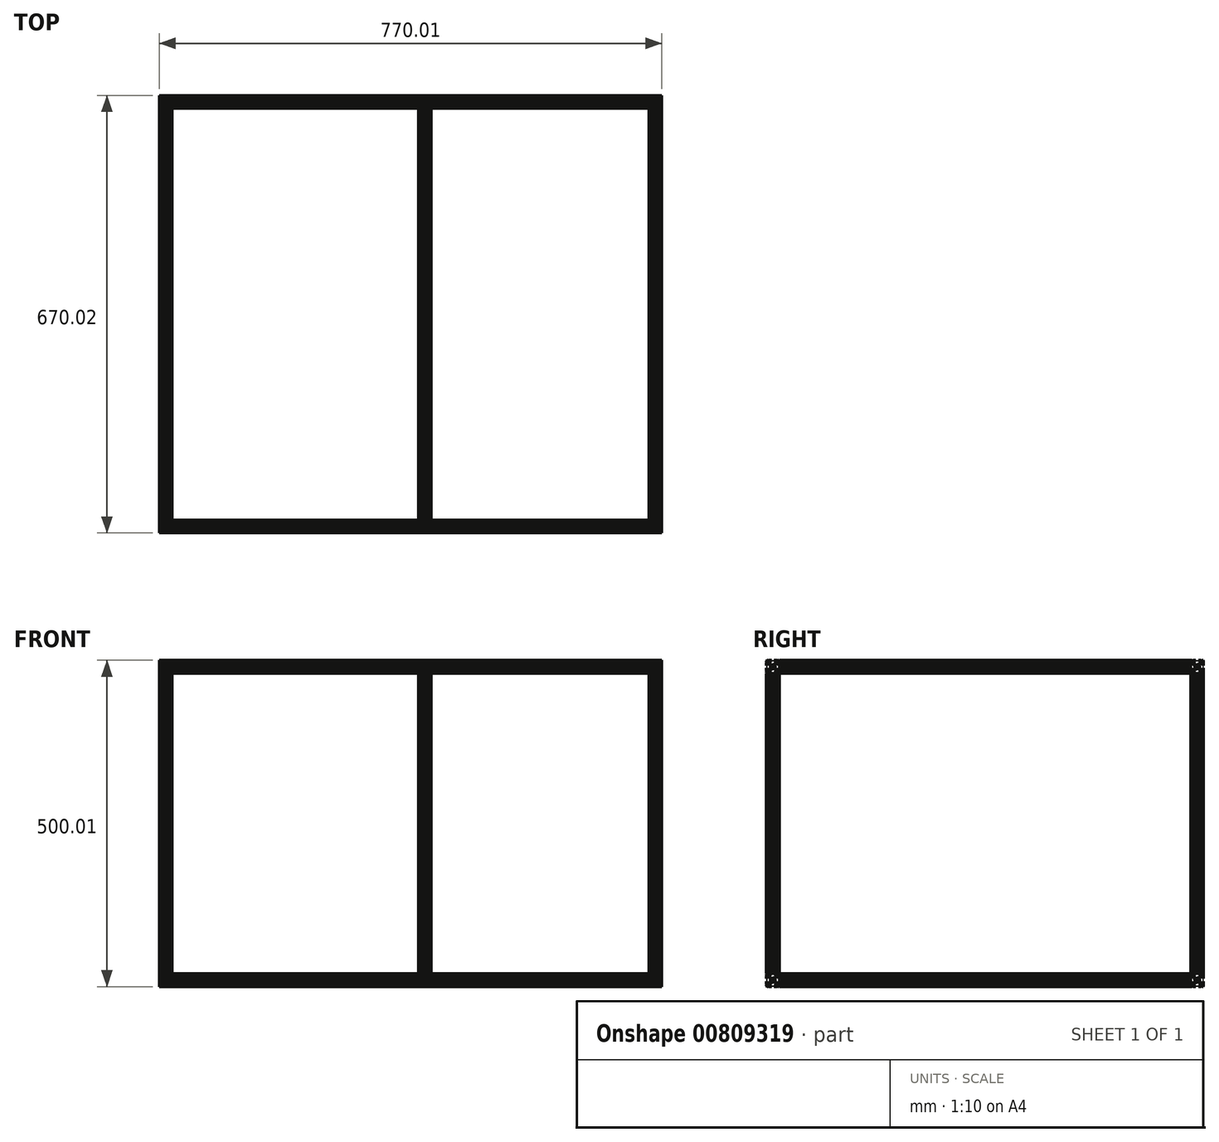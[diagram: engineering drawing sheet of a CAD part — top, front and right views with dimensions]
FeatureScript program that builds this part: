
annotation { "Feature Type Name" : "Feature", "Feature Type Description" : "" }
export const myFeature = defineFeature(function(context is Context, id is Id, definition is map)
    precondition{}
    {
        {
            var Q0;
            Q0=qCreatedBy(makeId("Right.planeOp"),FACE);
            var sketch = newSketch(context, id + "F0", { "sketchPlane" : qUnion([Q0])});
            skLineSegment(sketch, "E0", {"start": v(25.7, -17.22) * mm, "end": v(25.7, -25.12) * mm});
            skLineSegment(sketch, "E1", {"start": v(22.1, -21.63) * mm, "end": v(30.9, -21.63) * mm});
            skLineSegment(sketch, "E2", {"start": v(25.7, -40.02) * mm, "end": v(25.7, -32.12) * mm});
            skLineSegment(sketch, "E3", {"start": v(22.1, -35.63) * mm, "end": v(30.9, -35.63) * mm});
            skLineSegment(sketch, "E4", {"start": v(28.7, -30.77) * mm, "end": v(27.2, -30.77) * mm});
            skLineSegment(sketch, "E5", {"start": v(27.2, -32.77) * mm, "end": v(23.2, -32.77) * mm});
            skLineSegment(sketch, "E6", {"start": v(27.2, -32.77) * mm, "end": v(27.2, -30.77) * mm});
            skLineSegment(sketch, "E7", {"start": v(28.7, -26.48) * mm, "end": v(27.2, -26.48) * mm});
            skLineSegment(sketch, "E8", {"start": v(27.2, -24.48) * mm, "end": v(23.2, -24.48) * mm});
            skLineSegment(sketch, "E9", {"start": v(27.2, -24.48) * mm, "end": v(27.2, -26.48) * mm});
            skLineSegment(sketch, "E10", {"start": v(23.2, -24.48) * mm, "end": v(23.2, -26.12) * mm});
            skLineSegment(sketch, "E11", {"start": v(23.2, -26.12) * mm, "end": v(21.9, -26.12) * mm});
            skLineSegment(sketch, "E12", {"start": v(23.2, -32.77) * mm, "end": v(21.9, -26.12) * mm});
            skLineSegment(sketch, "E13", {"start": v(27.34, -20.94) * mm, "end": v(26.38, -19.97) * mm});
            skLineSegment(sketch, "E14", {"start": v(26.38, -19.97) * mm, "end": v(25, -19.97) * mm});
            skLineSegment(sketch, "E15", {"start": v(25, -19.97) * mm, "end": v(24.04, -20.94) * mm});
            skLineSegment(sketch, "E16", {"start": v(24.04, -20.94) * mm, "end": v(24.04, -22.3) * mm});
            skLineSegment(sketch, "E17", {"start": v(24.04, -22.3) * mm, "end": v(25, -23.28) * mm});
            skLineSegment(sketch, "E18", {"start": v(25, -23.28) * mm, "end": v(26.38, -23.28) * mm});
            skLineSegment(sketch, "E19", {"start": v(26.38, -23.28) * mm, "end": v(27.34, -22.3) * mm});
            skLineSegment(sketch, "E20", {"start": v(27.34, -22.3) * mm, "end": v(27.34, -20.94) * mm});
            skLineSegment(sketch, "E21", {"start": v(27.34, -34.94) * mm, "end": v(26.38, -33.98) * mm});
            skLineSegment(sketch, "E22", {"start": v(26.38, -33.98) * mm, "end": v(25, -33.98) * mm});
            skLineSegment(sketch, "E23", {"start": v(25, -33.98) * mm, "end": v(24.04, -34.94) * mm});
            skLineSegment(sketch, "E24", {"start": v(24.04, -34.94) * mm, "end": v(24.04, -36.3) * mm});
            skLineSegment(sketch, "E25", {"start": v(24.04, -36.3) * mm, "end": v(25, -37.28) * mm});
            skLineSegment(sketch, "E26", {"start": v(25, -37.28) * mm, "end": v(26.38, -37.28) * mm});
            skLineSegment(sketch, "E27", {"start": v(26.38, -37.28) * mm, "end": v(27.34, -36.3) * mm});
            skLineSegment(sketch, "E28", {"start": v(27.34, -36.3) * mm, "end": v(27.34, -34.94) * mm});
            skLineSegment(sketch, "E29", {"start": v(27.7, -18.62) * mm, "end": v(28.7, -19.62) * mm});
            skLineSegment(sketch, "E30", {"start": v(28.7, -37.62) * mm, "end": v(27.7, -38.62) * mm});
            skLineSegment(sketch, "E31", {"start": v(25.7, -18.83) * mm, "end": v(26.44, -18.83) * mm});
            skLineSegment(sketch, "E32", {"start": v(26.44, -18.83) * mm, "end": v(26.44, -18.62) * mm});
            skLineSegment(sketch, "E33", {"start": v(25.7, -18.83) * mm, "end": v(24.94, -18.83) * mm});
            skLineSegment(sketch, "E34", {"start": v(24.94, -18.83) * mm, "end": v(24.94, -18.62) * mm});
            skLineSegment(sketch, "E35", {"start": v(27.7, -18.62) * mm, "end": v(26.44, -18.62) * mm});
            skLineSegment(sketch, "E36", {"start": v(28.5, -21.63) * mm, "end": v(28.5, -22.38) * mm});
            skLineSegment(sketch, "E37", {"start": v(28.5, -22.38) * mm, "end": v(28.7, -22.38) * mm});
            skLineSegment(sketch, "E38", {"start": v(28.5, -21.63) * mm, "end": v(28.5, -20.88) * mm});
            skLineSegment(sketch, "E39", {"start": v(28.5, -20.88) * mm, "end": v(28.7, -20.88) * mm});
            skLineSegment(sketch, "E40", {"start": v(28.5, -35.63) * mm, "end": v(28.5, -34.88) * mm});
            skLineSegment(sketch, "E41", {"start": v(28.5, -34.88) * mm, "end": v(28.7, -34.88) * mm});
            skLineSegment(sketch, "E42", {"start": v(28.5, -35.63) * mm, "end": v(28.5, -36.38) * mm});
            skLineSegment(sketch, "E43", {"start": v(28.5, -36.38) * mm, "end": v(28.7, -36.38) * mm});
            skLineSegment(sketch, "E44", {"start": v(25.7, -38.43) * mm, "end": v(26.44, -38.43) * mm});
            skLineSegment(sketch, "E45", {"start": v(26.44, -38.43) * mm, "end": v(26.44, -38.62) * mm});
            skLineSegment(sketch, "E46", {"start": v(25.7, -38.43) * mm, "end": v(24.94, -38.43) * mm});
            skLineSegment(sketch, "E47", {"start": v(24.94, -38.43) * mm, "end": v(24.94, -38.62) * mm});
            skLineSegment(sketch, "E48", {"start": v(28.7, -19.62) * mm, "end": v(28.7, -20.88) * mm});
            skLineSegment(sketch, "E49", {"start": v(28.7, -22.38) * mm, "end": v(28.7, -26.48) * mm});
            skLineSegment(sketch, "E50", {"start": v(27.7, -38.62) * mm, "end": v(26.44, -38.62) * mm});
            skLineSegment(sketch, "E51", {"start": v(28.7, -37.62) * mm, "end": v(28.7, -36.38) * mm});
            skLineSegment(sketch, "E52", {"start": v(28.7, -34.88) * mm, "end": v(28.7, -30.77) * mm});
            skLineSegment(sketch, "E53", {"start": v(18.7, -13.92) * mm, "end": v(18.7, -42.92) * mm});
            skLineSegment(sketch, "E54", {"start": v(20.84, -18.62) * mm, "end": v(20.84, -20.12) * mm});
            skLineSegment(sketch, "E55", {"start": v(22.84, -20.12) * mm, "end": v(22.84, -24.12) * mm});
            skLineSegment(sketch, "E56", {"start": v(22.84, -20.12) * mm, "end": v(20.84, -20.12) * mm});
            skLineSegment(sketch, "E57", {"start": v(16.54, -18.62) * mm, "end": v(16.54, -20.12) * mm});
            skLineSegment(sketch, "E58", {"start": v(14.54, -20.12) * mm, "end": v(14.54, -24.12) * mm});
            skLineSegment(sketch, "E59", {"start": v(14.54, -20.12) * mm, "end": v(16.54, -20.12) * mm});
            skLineSegment(sketch, "E60", {"start": v(14.54, -24.12) * mm, "end": v(16.2, -24.12) * mm});
            skLineSegment(sketch, "E61", {"start": v(16.2, -24.12) * mm, "end": v(16.2, -25.42) * mm});
            skLineSegment(sketch, "E62", {"start": v(22.84, -24.12) * mm, "end": v(16.2, -25.42) * mm});
            skLineSegment(sketch, "E63", {"start": v(16.54, -38.62) * mm, "end": v(16.54, -37.12) * mm});
            skLineSegment(sketch, "E64", {"start": v(14.54, -37.12) * mm, "end": v(14.54, -33.12) * mm});
            skLineSegment(sketch, "E65", {"start": v(14.54, -37.12) * mm, "end": v(16.54, -37.12) * mm});
            skLineSegment(sketch, "E66", {"start": v(20.84, -38.62) * mm, "end": v(20.84, -37.12) * mm});
            skLineSegment(sketch, "E67", {"start": v(22.84, -37.12) * mm, "end": v(22.84, -33.12) * mm});
            skLineSegment(sketch, "E68", {"start": v(22.84, -37.12) * mm, "end": v(20.84, -37.12) * mm});
            skLineSegment(sketch, "E69", {"start": v(22.84, -33.12) * mm, "end": v(21.2, -33.12) * mm});
            skLineSegment(sketch, "E70", {"start": v(21.2, -33.12) * mm, "end": v(21.2, -31.83) * mm});
            skLineSegment(sketch, "E71", {"start": v(14.54, -33.12) * mm, "end": v(21.2, -31.83) * mm});
            skLineSegment(sketch, "E72", {"start": v(24.94, -18.62) * mm, "end": v(20.84, -18.62) * mm});
            skLineSegment(sketch, "E73", {"start": v(24.94, -38.62) * mm, "end": v(20.84, -38.62) * mm});
            skLineSegment(sketch, "E74", {"start": v(6.1, -28.62) * mm, "end": v(31.6, -28.62) * mm});
            skLineSegment(sketch, "E75", {"start": v(11.7, -17.22) * mm, "end": v(11.7, -25.12) * mm});
            skLineSegment(sketch, "E76", {"start": v(15.3, -21.63) * mm, "end": v(6.5, -21.63) * mm});
            skLineSegment(sketch, "E77", {"start": v(10.04, -20.94) * mm, "end": v(11, -19.97) * mm});
            skLineSegment(sketch, "E78", {"start": v(11, -19.97) * mm, "end": v(12.38, -19.97) * mm});
            skLineSegment(sketch, "E79", {"start": v(12.38, -19.97) * mm, "end": v(13.34, -20.94) * mm});
            skLineSegment(sketch, "E80", {"start": v(13.34, -20.94) * mm, "end": v(13.34, -22.3) * mm});
            skLineSegment(sketch, "E81", {"start": v(13.34, -22.3) * mm, "end": v(12.38, -23.28) * mm});
            skLineSegment(sketch, "E82", {"start": v(12.38, -23.28) * mm, "end": v(11, -23.28) * mm});
            skLineSegment(sketch, "E83", {"start": v(11, -23.28) * mm, "end": v(10.04, -22.3) * mm});
            skLineSegment(sketch, "E84", {"start": v(10.04, -22.3) * mm, "end": v(10.04, -20.94) * mm});
            skLineSegment(sketch, "E85", {"start": v(9.7, -18.62) * mm, "end": v(8.7, -19.62) * mm});
            skLineSegment(sketch, "E86", {"start": v(11.7, -18.83) * mm, "end": v(10.94, -18.83) * mm});
            skLineSegment(sketch, "E87", {"start": v(10.94, -18.83) * mm, "end": v(10.94, -18.62) * mm});
            skLineSegment(sketch, "E88", {"start": v(11.7, -18.83) * mm, "end": v(12.44, -18.83) * mm});
            skLineSegment(sketch, "E89", {"start": v(12.44, -18.83) * mm, "end": v(12.44, -18.62) * mm});
            skLineSegment(sketch, "E90", {"start": v(9.7, -18.62) * mm, "end": v(10.94, -18.62) * mm});
            skLineSegment(sketch, "E91", {"start": v(8.9, -21.63) * mm, "end": v(8.9, -22.38) * mm});
            skLineSegment(sketch, "E92", {"start": v(8.9, -22.38) * mm, "end": v(8.7, -22.38) * mm});
            skLineSegment(sketch, "E93", {"start": v(8.9, -21.63) * mm, "end": v(8.9, -20.88) * mm});
            skLineSegment(sketch, "E94", {"start": v(8.9, -20.88) * mm, "end": v(8.7, -20.88) * mm});
            skLineSegment(sketch, "E95", {"start": v(8.7, -19.62) * mm, "end": v(8.7, -20.88) * mm});
            skLineSegment(sketch, "E96", {"start": v(8.7, -22.38) * mm, "end": v(8.7, -26.48) * mm});
            skLineSegment(sketch, "E97", {"start": v(12.44, -18.62) * mm, "end": v(16.54, -18.62) * mm});
            skLineSegment(sketch, "E98", {"start": v(11.7, -40.02) * mm, "end": v(11.7, -32.12) * mm});
            skLineSegment(sketch, "E99", {"start": v(15.3, -35.63) * mm, "end": v(6.5, -35.63) * mm});
            skLineSegment(sketch, "E100", {"start": v(10.04, -34.94) * mm, "end": v(11, -33.98) * mm});
            skLineSegment(sketch, "E101", {"start": v(11, -33.98) * mm, "end": v(12.38, -33.98) * mm});
            skLineSegment(sketch, "E102", {"start": v(12.38, -33.98) * mm, "end": v(13.34, -34.94) * mm});
            skLineSegment(sketch, "E103", {"start": v(13.34, -34.94) * mm, "end": v(13.34, -36.3) * mm});
            skLineSegment(sketch, "E104", {"start": v(13.34, -36.3) * mm, "end": v(12.38, -37.28) * mm});
            skLineSegment(sketch, "E105", {"start": v(12.38, -37.28) * mm, "end": v(11, -37.28) * mm});
            skLineSegment(sketch, "E106", {"start": v(11, -37.28) * mm, "end": v(10.04, -36.3) * mm});
            skLineSegment(sketch, "E107", {"start": v(10.04, -36.3) * mm, "end": v(10.04, -34.94) * mm});
            skLineSegment(sketch, "E108", {"start": v(8.7, -37.62) * mm, "end": v(9.7, -38.62) * mm});
            skLineSegment(sketch, "E109", {"start": v(8.9, -35.63) * mm, "end": v(8.9, -34.88) * mm});
            skLineSegment(sketch, "E110", {"start": v(8.9, -34.88) * mm, "end": v(8.7, -34.88) * mm});
            skLineSegment(sketch, "E111", {"start": v(8.9, -35.63) * mm, "end": v(8.9, -36.38) * mm});
            skLineSegment(sketch, "E112", {"start": v(8.9, -36.38) * mm, "end": v(8.7, -36.38) * mm});
            skLineSegment(sketch, "E113", {"start": v(11.7, -38.43) * mm, "end": v(10.94, -38.43) * mm});
            skLineSegment(sketch, "E114", {"start": v(10.94, -38.43) * mm, "end": v(10.94, -38.62) * mm});
            skLineSegment(sketch, "E115", {"start": v(11.7, -38.43) * mm, "end": v(12.44, -38.43) * mm});
            skLineSegment(sketch, "E116", {"start": v(12.44, -38.43) * mm, "end": v(12.44, -38.62) * mm});
            skLineSegment(sketch, "E117", {"start": v(9.7, -38.62) * mm, "end": v(10.94, -38.62) * mm});
            skLineSegment(sketch, "E118", {"start": v(8.7, -37.62) * mm, "end": v(8.7, -36.38) * mm});
            skLineSegment(sketch, "E119", {"start": v(8.7, -34.88) * mm, "end": v(8.7, -30.77) * mm});
            skLineSegment(sketch, "E120", {"start": v(12.44, -38.62) * mm, "end": v(16.54, -38.62) * mm});
            skLineSegment(sketch, "E121", {"start": v(8.7, -26.48) * mm, "end": v(10.2, -26.48) * mm});
            skLineSegment(sketch, "E122", {"start": v(10.2, -24.48) * mm, "end": v(14.2, -24.48) * mm});
            skLineSegment(sketch, "E123", {"start": v(10.2, -24.48) * mm, "end": v(10.2, -26.48) * mm});
            skLineSegment(sketch, "E124", {"start": v(8.7, -30.77) * mm, "end": v(10.2, -30.77) * mm});
            skLineSegment(sketch, "E125", {"start": v(10.2, -32.77) * mm, "end": v(14.2, -32.77) * mm});
            skLineSegment(sketch, "E126", {"start": v(10.2, -32.77) * mm, "end": v(10.2, -30.77) * mm});
            skLineSegment(sketch, "E127", {"start": v(14.2, -32.77) * mm, "end": v(14.2, -31.12) * mm});
            skLineSegment(sketch, "E128", {"start": v(14.2, -31.12) * mm, "end": v(15.5, -31.12) * mm});
            skLineSegment(sketch, "E129", {"start": v(14.2, -24.48) * mm, "end": v(15.5, -31.12) * mm});
            skCircle(sketch, "E130", {"center": v(18.7, -28.62) * mm, "radius": 1.6 * mm});
            skSolve(sketch);
        }
        {
            var Q0;
            Q0 = qSketchRegion(id + "F0", true);
            extrude(context, id + "F1", {"entities" : qUnion([Q0]), "oppositeDirection" : true, "depth" : 770 * mm, "offsetDistance" : 25 * mm});
        }
        {
            var Q0;
            Q0=makeQuery(id+"F1.opExtrude","SWEPT_BODY",BODY,{"disambiguationData":[OSD([sQuery(id+"F0.wireOp",EDGE,"E4"),sQuery(id+"F0.wireOp",EDGE,"E5"),sQuery(id+"F0.wireOp",EDGE,"E6"),sQuery(id+"F0.wireOp",EDGE,"E7"),sQuery(id+"F0.wireOp",EDGE,"E8"),sQuery(id+"F0.wireOp",EDGE,"E9"),sQuery(id+"F0.wireOp",EDGE,"E10"),sQuery(id+"F0.wireOp",EDGE,"E11"),sQuery(id+"F0.wireOp",EDGE,"E12"),sQuery(id+"F0.wireOp",EDGE,"E13"),sQuery(id+"F0.wireOp",EDGE,"E14"),sQuery(id+"F0.wireOp",EDGE,"E15"),sQuery(id+"F0.wireOp",EDGE,"E16"),sQuery(id+"F0.wireOp",EDGE,"E17"),sQuery(id+"F0.wireOp",EDGE,"E18"),sQuery(id+"F0.wireOp",EDGE,"E19"),sQuery(id+"F0.wireOp",EDGE,"E20"),sQuery(id+"F0.wireOp",EDGE,"E21"),sQuery(id+"F0.wireOp",EDGE,"E22"),sQuery(id+"F0.wireOp",EDGE,"E23"),sQuery(id+"F0.wireOp",EDGE,"E24"),sQuery(id+"F0.wireOp",EDGE,"E25"),sQuery(id+"F0.wireOp",EDGE,"E26"),sQuery(id+"F0.wireOp",EDGE,"E27"),sQuery(id+"F0.wireOp",EDGE,"E28"),sQuery(id+"F0.wireOp",EDGE,"E29"),sQuery(id+"F0.wireOp",EDGE,"E30"),sQuery(id+"F0.wireOp",EDGE,"E31"),sQuery(id+"F0.wireOp",EDGE,"E32"),sQuery(id+"F0.wireOp",EDGE,"E33"),sQuery(id+"F0.wireOp",EDGE,"E34"),sQuery(id+"F0.wireOp",EDGE,"E35"),sQuery(id+"F0.wireOp",EDGE,"E36"),sQuery(id+"F0.wireOp",EDGE,"E37"),sQuery(id+"F0.wireOp",EDGE,"E38"),sQuery(id+"F0.wireOp",EDGE,"E39"),sQuery(id+"F0.wireOp",EDGE,"E40"),sQuery(id+"F0.wireOp",EDGE,"E41"),sQuery(id+"F0.wireOp",EDGE,"E42"),sQuery(id+"F0.wireOp",EDGE,"E43"),sQuery(id+"F0.wireOp",EDGE,"E44"),sQuery(id+"F0.wireOp",EDGE,"E45"),sQuery(id+"F0.wireOp",EDGE,"E46"),sQuery(id+"F0.wireOp",EDGE,"E47"),sQuery(id+"F0.wireOp",EDGE,"E48"),sQuery(id+"F0.wireOp",EDGE,"E49"),sQuery(id+"F0.wireOp",EDGE,"E50"),sQuery(id+"F0.wireOp",EDGE,"E51"),sQuery(id+"F0.wireOp",EDGE,"E52"),sQuery(id+"F0.wireOp",EDGE,"E54"),sQuery(id+"F0.wireOp",EDGE,"E55"),sQuery(id+"F0.wireOp",EDGE,"E56"),sQuery(id+"F0.wireOp",EDGE,"E57"),sQuery(id+"F0.wireOp",EDGE,"E58"),sQuery(id+"F0.wireOp",EDGE,"E59"),sQuery(id+"F0.wireOp",EDGE,"E60"),sQuery(id+"F0.wireOp",EDGE,"E61"),sQuery(id+"F0.wireOp",EDGE,"E62"),sQuery(id+"F0.wireOp",EDGE,"E63"),sQuery(id+"F0.wireOp",EDGE,"E64"),sQuery(id+"F0.wireOp",EDGE,"E65"),sQuery(id+"F0.wireOp",EDGE,"E66"),sQuery(id+"F0.wireOp",EDGE,"E67"),sQuery(id+"F0.wireOp",EDGE,"E68"),sQuery(id+"F0.wireOp",EDGE,"E69"),sQuery(id+"F0.wireOp",EDGE,"E70"),sQuery(id+"F0.wireOp",EDGE,"E71"),sQuery(id+"F0.wireOp",EDGE,"E72"),sQuery(id+"F0.wireOp",EDGE,"E73"),sQuery(id+"F0.wireOp",EDGE,"E77"),sQuery(id+"F0.wireOp",EDGE,"E78"),sQuery(id+"F0.wireOp",EDGE,"E79"),sQuery(id+"F0.wireOp",EDGE,"E80"),sQuery(id+"F0.wireOp",EDGE,"E81"),sQuery(id+"F0.wireOp",EDGE,"E82"),sQuery(id+"F0.wireOp",EDGE,"E83"),sQuery(id+"F0.wireOp",EDGE,"E84"),sQuery(id+"F0.wireOp",EDGE,"E85"),sQuery(id+"F0.wireOp",EDGE,"E86"),sQuery(id+"F0.wireOp",EDGE,"E87"),sQuery(id+"F0.wireOp",EDGE,"E88"),sQuery(id+"F0.wireOp",EDGE,"E89"),sQuery(id+"F0.wireOp",EDGE,"E90"),sQuery(id+"F0.wireOp",EDGE,"E91"),sQuery(id+"F0.wireOp",EDGE,"E92"),sQuery(id+"F0.wireOp",EDGE,"E93"),sQuery(id+"F0.wireOp",EDGE,"E94"),sQuery(id+"F0.wireOp",EDGE,"E95"),sQuery(id+"F0.wireOp",EDGE,"E96"),sQuery(id+"F0.wireOp",EDGE,"E97"),sQuery(id+"F0.wireOp",EDGE,"E100"),sQuery(id+"F0.wireOp",EDGE,"E101"),sQuery(id+"F0.wireOp",EDGE,"E102"),sQuery(id+"F0.wireOp",EDGE,"E103"),sQuery(id+"F0.wireOp",EDGE,"E104"),sQuery(id+"F0.wireOp",EDGE,"E105"),sQuery(id+"F0.wireOp",EDGE,"E106"),sQuery(id+"F0.wireOp",EDGE,"E107"),sQuery(id+"F0.wireOp",EDGE,"E108"),sQuery(id+"F0.wireOp",EDGE,"E109"),sQuery(id+"F0.wireOp",EDGE,"E110"),sQuery(id+"F0.wireOp",EDGE,"E111"),sQuery(id+"F0.wireOp",EDGE,"E112"),sQuery(id+"F0.wireOp",EDGE,"E113"),sQuery(id+"F0.wireOp",EDGE,"E114"),sQuery(id+"F0.wireOp",EDGE,"E115"),sQuery(id+"F0.wireOp",EDGE,"E116"),sQuery(id+"F0.wireOp",EDGE,"E117"),sQuery(id+"F0.wireOp",EDGE,"E118"),sQuery(id+"F0.wireOp",EDGE,"E119"),sQuery(id+"F0.wireOp",EDGE,"E120"),sQuery(id+"F0.wireOp",EDGE,"E121"),sQuery(id+"F0.wireOp",EDGE,"E122"),sQuery(id+"F0.wireOp",EDGE,"E123"),sQuery(id+"F0.wireOp",EDGE,"E124"),sQuery(id+"F0.wireOp",EDGE,"E125"),sQuery(id+"F0.wireOp",EDGE,"E126"),sQuery(id+"F0.wireOp",EDGE,"E127"),sQuery(id+"F0.wireOp",EDGE,"E128"),sQuery(id+"F0.wireOp",EDGE,"E129"),sQuery(id+"F0.wireOp",EDGE,"E130")])]});
            transform(context, id + "F2", {"entities" : qUnion([Q0]), "transformType" : TransformType.TRANSLATION_3D, "dx" : 0 * mm, "dy" : 650 * mm, "dz" : 0 * mm, "makeCopy" : true});
        }
        {
            var Q0;
            Q0=makeQuery(id+"F1.opExtrude","SWEPT_BODY",BODY,{"disambiguationData":[OSD([sQuery(id+"F0.wireOp",EDGE,"E4"),sQuery(id+"F0.wireOp",EDGE,"E5"),sQuery(id+"F0.wireOp",EDGE,"E6"),sQuery(id+"F0.wireOp",EDGE,"E7"),sQuery(id+"F0.wireOp",EDGE,"E8"),sQuery(id+"F0.wireOp",EDGE,"E9"),sQuery(id+"F0.wireOp",EDGE,"E10"),sQuery(id+"F0.wireOp",EDGE,"E11"),sQuery(id+"F0.wireOp",EDGE,"E12"),sQuery(id+"F0.wireOp",EDGE,"E13"),sQuery(id+"F0.wireOp",EDGE,"E14"),sQuery(id+"F0.wireOp",EDGE,"E15"),sQuery(id+"F0.wireOp",EDGE,"E16"),sQuery(id+"F0.wireOp",EDGE,"E17"),sQuery(id+"F0.wireOp",EDGE,"E18"),sQuery(id+"F0.wireOp",EDGE,"E19"),sQuery(id+"F0.wireOp",EDGE,"E20"),sQuery(id+"F0.wireOp",EDGE,"E21"),sQuery(id+"F0.wireOp",EDGE,"E22"),sQuery(id+"F0.wireOp",EDGE,"E23"),sQuery(id+"F0.wireOp",EDGE,"E24"),sQuery(id+"F0.wireOp",EDGE,"E25"),sQuery(id+"F0.wireOp",EDGE,"E26"),sQuery(id+"F0.wireOp",EDGE,"E27"),sQuery(id+"F0.wireOp",EDGE,"E28"),sQuery(id+"F0.wireOp",EDGE,"E29"),sQuery(id+"F0.wireOp",EDGE,"E30"),sQuery(id+"F0.wireOp",EDGE,"E31"),sQuery(id+"F0.wireOp",EDGE,"E32"),sQuery(id+"F0.wireOp",EDGE,"E33"),sQuery(id+"F0.wireOp",EDGE,"E34"),sQuery(id+"F0.wireOp",EDGE,"E35"),sQuery(id+"F0.wireOp",EDGE,"E36"),sQuery(id+"F0.wireOp",EDGE,"E37"),sQuery(id+"F0.wireOp",EDGE,"E38"),sQuery(id+"F0.wireOp",EDGE,"E39"),sQuery(id+"F0.wireOp",EDGE,"E40"),sQuery(id+"F0.wireOp",EDGE,"E41"),sQuery(id+"F0.wireOp",EDGE,"E42"),sQuery(id+"F0.wireOp",EDGE,"E43"),sQuery(id+"F0.wireOp",EDGE,"E44"),sQuery(id+"F0.wireOp",EDGE,"E45"),sQuery(id+"F0.wireOp",EDGE,"E46"),sQuery(id+"F0.wireOp",EDGE,"E47"),sQuery(id+"F0.wireOp",EDGE,"E48"),sQuery(id+"F0.wireOp",EDGE,"E49"),sQuery(id+"F0.wireOp",EDGE,"E50"),sQuery(id+"F0.wireOp",EDGE,"E51"),sQuery(id+"F0.wireOp",EDGE,"E52"),sQuery(id+"F0.wireOp",EDGE,"E54"),sQuery(id+"F0.wireOp",EDGE,"E55"),sQuery(id+"F0.wireOp",EDGE,"E56"),sQuery(id+"F0.wireOp",EDGE,"E57"),sQuery(id+"F0.wireOp",EDGE,"E58"),sQuery(id+"F0.wireOp",EDGE,"E59"),sQuery(id+"F0.wireOp",EDGE,"E60"),sQuery(id+"F0.wireOp",EDGE,"E61"),sQuery(id+"F0.wireOp",EDGE,"E62"),sQuery(id+"F0.wireOp",EDGE,"E63"),sQuery(id+"F0.wireOp",EDGE,"E64"),sQuery(id+"F0.wireOp",EDGE,"E65"),sQuery(id+"F0.wireOp",EDGE,"E66"),sQuery(id+"F0.wireOp",EDGE,"E67"),sQuery(id+"F0.wireOp",EDGE,"E68"),sQuery(id+"F0.wireOp",EDGE,"E69"),sQuery(id+"F0.wireOp",EDGE,"E70"),sQuery(id+"F0.wireOp",EDGE,"E71"),sQuery(id+"F0.wireOp",EDGE,"E72"),sQuery(id+"F0.wireOp",EDGE,"E73"),sQuery(id+"F0.wireOp",EDGE,"E77"),sQuery(id+"F0.wireOp",EDGE,"E78"),sQuery(id+"F0.wireOp",EDGE,"E79"),sQuery(id+"F0.wireOp",EDGE,"E80"),sQuery(id+"F0.wireOp",EDGE,"E81"),sQuery(id+"F0.wireOp",EDGE,"E82"),sQuery(id+"F0.wireOp",EDGE,"E83"),sQuery(id+"F0.wireOp",EDGE,"E84"),sQuery(id+"F0.wireOp",EDGE,"E85"),sQuery(id+"F0.wireOp",EDGE,"E86"),sQuery(id+"F0.wireOp",EDGE,"E87"),sQuery(id+"F0.wireOp",EDGE,"E88"),sQuery(id+"F0.wireOp",EDGE,"E89"),sQuery(id+"F0.wireOp",EDGE,"E90"),sQuery(id+"F0.wireOp",EDGE,"E91"),sQuery(id+"F0.wireOp",EDGE,"E92"),sQuery(id+"F0.wireOp",EDGE,"E93"),sQuery(id+"F0.wireOp",EDGE,"E94"),sQuery(id+"F0.wireOp",EDGE,"E95"),sQuery(id+"F0.wireOp",EDGE,"E96"),sQuery(id+"F0.wireOp",EDGE,"E97"),sQuery(id+"F0.wireOp",EDGE,"E100"),sQuery(id+"F0.wireOp",EDGE,"E101"),sQuery(id+"F0.wireOp",EDGE,"E102"),sQuery(id+"F0.wireOp",EDGE,"E103"),sQuery(id+"F0.wireOp",EDGE,"E104"),sQuery(id+"F0.wireOp",EDGE,"E105"),sQuery(id+"F0.wireOp",EDGE,"E106"),sQuery(id+"F0.wireOp",EDGE,"E107"),sQuery(id+"F0.wireOp",EDGE,"E108"),sQuery(id+"F0.wireOp",EDGE,"E109"),sQuery(id+"F0.wireOp",EDGE,"E110"),sQuery(id+"F0.wireOp",EDGE,"E111"),sQuery(id+"F0.wireOp",EDGE,"E112"),sQuery(id+"F0.wireOp",EDGE,"E113"),sQuery(id+"F0.wireOp",EDGE,"E114"),sQuery(id+"F0.wireOp",EDGE,"E115"),sQuery(id+"F0.wireOp",EDGE,"E116"),sQuery(id+"F0.wireOp",EDGE,"E117"),sQuery(id+"F0.wireOp",EDGE,"E118"),sQuery(id+"F0.wireOp",EDGE,"E119"),sQuery(id+"F0.wireOp",EDGE,"E120"),sQuery(id+"F0.wireOp",EDGE,"E121"),sQuery(id+"F0.wireOp",EDGE,"E122"),sQuery(id+"F0.wireOp",EDGE,"E123"),sQuery(id+"F0.wireOp",EDGE,"E124"),sQuery(id+"F0.wireOp",EDGE,"E125"),sQuery(id+"F0.wireOp",EDGE,"E126"),sQuery(id+"F0.wireOp",EDGE,"E127"),sQuery(id+"F0.wireOp",EDGE,"E128"),sQuery(id+"F0.wireOp",EDGE,"E129"),sQuery(id+"F0.wireOp",EDGE,"E130")])]});
            var Q1;
            Q1=makeQuery(id+"F2.opPattern","COPY",BODY,{"derivedFrom":makeQuery(id+"F1.opExtrude","SWEPT_BODY",BODY,{"disambiguationData":[OSD([sQuery(id+"F0.wireOp",EDGE,"E4"),sQuery(id+"F0.wireOp",EDGE,"E5"),sQuery(id+"F0.wireOp",EDGE,"E6"),sQuery(id+"F0.wireOp",EDGE,"E7"),sQuery(id+"F0.wireOp",EDGE,"E8"),sQuery(id+"F0.wireOp",EDGE,"E9"),sQuery(id+"F0.wireOp",EDGE,"E10"),sQuery(id+"F0.wireOp",EDGE,"E11"),sQuery(id+"F0.wireOp",EDGE,"E12"),sQuery(id+"F0.wireOp",EDGE,"E13"),sQuery(id+"F0.wireOp",EDGE,"E14"),sQuery(id+"F0.wireOp",EDGE,"E15"),sQuery(id+"F0.wireOp",EDGE,"E16"),sQuery(id+"F0.wireOp",EDGE,"E17"),sQuery(id+"F0.wireOp",EDGE,"E18"),sQuery(id+"F0.wireOp",EDGE,"E19"),sQuery(id+"F0.wireOp",EDGE,"E20"),sQuery(id+"F0.wireOp",EDGE,"E21"),sQuery(id+"F0.wireOp",EDGE,"E22"),sQuery(id+"F0.wireOp",EDGE,"E23"),sQuery(id+"F0.wireOp",EDGE,"E24"),sQuery(id+"F0.wireOp",EDGE,"E25"),sQuery(id+"F0.wireOp",EDGE,"E26"),sQuery(id+"F0.wireOp",EDGE,"E27"),sQuery(id+"F0.wireOp",EDGE,"E28"),sQuery(id+"F0.wireOp",EDGE,"E29"),sQuery(id+"F0.wireOp",EDGE,"E30"),sQuery(id+"F0.wireOp",EDGE,"E31"),sQuery(id+"F0.wireOp",EDGE,"E32"),sQuery(id+"F0.wireOp",EDGE,"E33"),sQuery(id+"F0.wireOp",EDGE,"E34"),sQuery(id+"F0.wireOp",EDGE,"E35"),sQuery(id+"F0.wireOp",EDGE,"E36"),sQuery(id+"F0.wireOp",EDGE,"E37"),sQuery(id+"F0.wireOp",EDGE,"E38"),sQuery(id+"F0.wireOp",EDGE,"E39"),sQuery(id+"F0.wireOp",EDGE,"E40"),sQuery(id+"F0.wireOp",EDGE,"E41"),sQuery(id+"F0.wireOp",EDGE,"E42"),sQuery(id+"F0.wireOp",EDGE,"E43"),sQuery(id+"F0.wireOp",EDGE,"E44"),sQuery(id+"F0.wireOp",EDGE,"E45"),sQuery(id+"F0.wireOp",EDGE,"E46"),sQuery(id+"F0.wireOp",EDGE,"E47"),sQuery(id+"F0.wireOp",EDGE,"E48"),sQuery(id+"F0.wireOp",EDGE,"E49"),sQuery(id+"F0.wireOp",EDGE,"E50"),sQuery(id+"F0.wireOp",EDGE,"E51"),sQuery(id+"F0.wireOp",EDGE,"E52"),sQuery(id+"F0.wireOp",EDGE,"E54"),sQuery(id+"F0.wireOp",EDGE,"E55"),sQuery(id+"F0.wireOp",EDGE,"E56"),sQuery(id+"F0.wireOp",EDGE,"E57"),sQuery(id+"F0.wireOp",EDGE,"E58"),sQuery(id+"F0.wireOp",EDGE,"E59"),sQuery(id+"F0.wireOp",EDGE,"E60"),sQuery(id+"F0.wireOp",EDGE,"E61"),sQuery(id+"F0.wireOp",EDGE,"E62"),sQuery(id+"F0.wireOp",EDGE,"E63"),sQuery(id+"F0.wireOp",EDGE,"E64"),sQuery(id+"F0.wireOp",EDGE,"E65"),sQuery(id+"F0.wireOp",EDGE,"E66"),sQuery(id+"F0.wireOp",EDGE,"E67"),sQuery(id+"F0.wireOp",EDGE,"E68"),sQuery(id+"F0.wireOp",EDGE,"E69"),sQuery(id+"F0.wireOp",EDGE,"E70"),sQuery(id+"F0.wireOp",EDGE,"E71"),sQuery(id+"F0.wireOp",EDGE,"E72"),sQuery(id+"F0.wireOp",EDGE,"E73"),sQuery(id+"F0.wireOp",EDGE,"E77"),sQuery(id+"F0.wireOp",EDGE,"E78"),sQuery(id+"F0.wireOp",EDGE,"E79"),sQuery(id+"F0.wireOp",EDGE,"E80"),sQuery(id+"F0.wireOp",EDGE,"E81"),sQuery(id+"F0.wireOp",EDGE,"E82"),sQuery(id+"F0.wireOp",EDGE,"E83"),sQuery(id+"F0.wireOp",EDGE,"E84"),sQuery(id+"F0.wireOp",EDGE,"E85"),sQuery(id+"F0.wireOp",EDGE,"E86"),sQuery(id+"F0.wireOp",EDGE,"E87"),sQuery(id+"F0.wireOp",EDGE,"E88"),sQuery(id+"F0.wireOp",EDGE,"E89"),sQuery(id+"F0.wireOp",EDGE,"E90"),sQuery(id+"F0.wireOp",EDGE,"E91"),sQuery(id+"F0.wireOp",EDGE,"E92"),sQuery(id+"F0.wireOp",EDGE,"E93"),sQuery(id+"F0.wireOp",EDGE,"E94"),sQuery(id+"F0.wireOp",EDGE,"E95"),sQuery(id+"F0.wireOp",EDGE,"E96"),sQuery(id+"F0.wireOp",EDGE,"E97"),sQuery(id+"F0.wireOp",EDGE,"E100"),sQuery(id+"F0.wireOp",EDGE,"E101"),sQuery(id+"F0.wireOp",EDGE,"E102"),sQuery(id+"F0.wireOp",EDGE,"E103"),sQuery(id+"F0.wireOp",EDGE,"E104"),sQuery(id+"F0.wireOp",EDGE,"E105"),sQuery(id+"F0.wireOp",EDGE,"E106"),sQuery(id+"F0.wireOp",EDGE,"E107"),sQuery(id+"F0.wireOp",EDGE,"E108"),sQuery(id+"F0.wireOp",EDGE,"E109"),sQuery(id+"F0.wireOp",EDGE,"E110"),sQuery(id+"F0.wireOp",EDGE,"E111"),sQuery(id+"F0.wireOp",EDGE,"E112"),sQuery(id+"F0.wireOp",EDGE,"E113"),sQuery(id+"F0.wireOp",EDGE,"E114"),sQuery(id+"F0.wireOp",EDGE,"E115"),sQuery(id+"F0.wireOp",EDGE,"E116"),sQuery(id+"F0.wireOp",EDGE,"E117"),sQuery(id+"F0.wireOp",EDGE,"E118"),sQuery(id+"F0.wireOp",EDGE,"E119"),sQuery(id+"F0.wireOp",EDGE,"E120"),sQuery(id+"F0.wireOp",EDGE,"E121"),sQuery(id+"F0.wireOp",EDGE,"E122"),sQuery(id+"F0.wireOp",EDGE,"E123"),sQuery(id+"F0.wireOp",EDGE,"E124"),sQuery(id+"F0.wireOp",EDGE,"E125"),sQuery(id+"F0.wireOp",EDGE,"E126"),sQuery(id+"F0.wireOp",EDGE,"E127"),sQuery(id+"F0.wireOp",EDGE,"E128"),sQuery(id+"F0.wireOp",EDGE,"E129"),sQuery(id+"F0.wireOp",EDGE,"E130")])]}),"instanceName":"1"});
            transform(context, id + "F3", {"entities" : qUnion([Q0, Q1]), "transformType" : TransformType.TRANSLATION_3D, "dx" : 0 * mm, "dy" : 0 * mm, "dz" : 480 * mm, "makeCopy" : true});
        }
        {
            var Q0;
            Q0=qCreatedBy(makeId("Front.planeOp"),FACE);
            cPlane(context, id + "F4", {"entities" : qUnion([Q0]), "cplaneType" : CPlaneType.OFFSET, "offset" : 8.7 * mm, "oppositeDirection" : true, "width" : 150 * mm, "height" : 150 * mm});
        }
        {
            var Q0;
            Q0=qCreatedBy(id+"F4.planeOp",FACE);
            cPlane(context, id + "F5", {"entities" : qUnion([Q0]), "cplaneType" : CPlaneType.OFFSET, "offset" : 650 * mm, "oppositeDirection" : true, "width" : 150 * mm, "height" : 150 * mm});
        }
        {
            var Q0;
            Q0=qCreatedBy(id+"F5.planeOp",FACE);
            var sketch = newSketch(context, id + "F6", { "sketchPlane" : qUnion([Q0])});
            skLineSegment(sketch, "E131", {"start": v(25.7, -17.22) * mm, "end": v(25.7, -25.12) * mm});
            skLineSegment(sketch, "E132", {"start": v(22.1, -21.63) * mm, "end": v(30.9, -21.63) * mm});
            skLineSegment(sketch, "E133", {"start": v(25.7, -40.02) * mm, "end": v(25.7, -32.12) * mm});
            skLineSegment(sketch, "E134", {"start": v(22.1, -35.63) * mm, "end": v(30.9, -35.63) * mm});
            skLineSegment(sketch, "E135", {"start": v(28.7, -30.77) * mm, "end": v(27.2, -30.77) * mm});
            skLineSegment(sketch, "E136", {"start": v(27.2, -32.77) * mm, "end": v(23.2, -32.77) * mm});
            skLineSegment(sketch, "E137", {"start": v(27.2, -32.77) * mm, "end": v(27.2, -30.77) * mm});
            skLineSegment(sketch, "E138", {"start": v(28.7, -26.48) * mm, "end": v(27.2, -26.48) * mm});
            skLineSegment(sketch, "E139", {"start": v(27.2, -24.48) * mm, "end": v(23.2, -24.48) * mm});
            skLineSegment(sketch, "E140", {"start": v(27.2, -24.48) * mm, "end": v(27.2, -26.48) * mm});
            skLineSegment(sketch, "E141", {"start": v(23.2, -24.48) * mm, "end": v(23.2, -26.12) * mm});
            skLineSegment(sketch, "E142", {"start": v(23.2, -26.12) * mm, "end": v(21.9, -26.12) * mm});
            skLineSegment(sketch, "E143", {"start": v(23.2, -32.77) * mm, "end": v(21.9, -26.12) * mm});
            skLineSegment(sketch, "E144", {"start": v(27.34, -20.94) * mm, "end": v(26.38, -19.97) * mm});
            skLineSegment(sketch, "E145", {"start": v(26.38, -19.97) * mm, "end": v(25, -19.97) * mm});
            skLineSegment(sketch, "E146", {"start": v(25, -19.97) * mm, "end": v(24.04, -20.94) * mm});
            skLineSegment(sketch, "E147", {"start": v(24.04, -20.94) * mm, "end": v(24.04, -22.3) * mm});
            skLineSegment(sketch, "E148", {"start": v(24.04, -22.3) * mm, "end": v(25, -23.28) * mm});
            skLineSegment(sketch, "E149", {"start": v(25, -23.28) * mm, "end": v(26.38, -23.28) * mm});
            skLineSegment(sketch, "E150", {"start": v(26.38, -23.28) * mm, "end": v(27.34, -22.3) * mm});
            skLineSegment(sketch, "E151", {"start": v(27.34, -22.3) * mm, "end": v(27.34, -20.94) * mm});
            skLineSegment(sketch, "E152", {"start": v(27.34, -34.94) * mm, "end": v(26.38, -33.98) * mm});
            skLineSegment(sketch, "E153", {"start": v(26.38, -33.98) * mm, "end": v(25, -33.98) * mm});
            skLineSegment(sketch, "E154", {"start": v(25, -33.98) * mm, "end": v(24.04, -34.94) * mm});
            skLineSegment(sketch, "E155", {"start": v(24.04, -34.94) * mm, "end": v(24.04, -36.3) * mm});
            skLineSegment(sketch, "E156", {"start": v(24.04, -36.3) * mm, "end": v(25, -37.28) * mm});
            skLineSegment(sketch, "E157", {"start": v(25, -37.28) * mm, "end": v(26.38, -37.28) * mm});
            skLineSegment(sketch, "E158", {"start": v(26.38, -37.28) * mm, "end": v(27.34, -36.3) * mm});
            skLineSegment(sketch, "E159", {"start": v(27.34, -36.3) * mm, "end": v(27.34, -34.94) * mm});
            skLineSegment(sketch, "E160", {"start": v(27.7, -18.62) * mm, "end": v(28.7, -19.62) * mm});
            skLineSegment(sketch, "E161", {"start": v(28.7, -37.62) * mm, "end": v(27.7, -38.62) * mm});
            skLineSegment(sketch, "E162", {"start": v(25.7, -18.83) * mm, "end": v(26.44, -18.83) * mm});
            skLineSegment(sketch, "E163", {"start": v(26.44, -18.83) * mm, "end": v(26.44, -18.62) * mm});
            skLineSegment(sketch, "E164", {"start": v(25.7, -18.83) * mm, "end": v(24.94, -18.83) * mm});
            skLineSegment(sketch, "E165", {"start": v(24.94, -18.83) * mm, "end": v(24.94, -18.62) * mm});
            skLineSegment(sketch, "E166", {"start": v(27.7, -18.62) * mm, "end": v(26.44, -18.62) * mm});
            skLineSegment(sketch, "E167", {"start": v(28.5, -21.63) * mm, "end": v(28.5, -22.38) * mm});
            skLineSegment(sketch, "E168", {"start": v(28.5, -22.38) * mm, "end": v(28.7, -22.38) * mm});
            skLineSegment(sketch, "E169", {"start": v(28.5, -21.63) * mm, "end": v(28.5, -20.88) * mm});
            skLineSegment(sketch, "E170", {"start": v(28.5, -20.88) * mm, "end": v(28.7, -20.88) * mm});
            skLineSegment(sketch, "E171", {"start": v(28.5, -35.63) * mm, "end": v(28.5, -34.88) * mm});
            skLineSegment(sketch, "E172", {"start": v(28.5, -34.88) * mm, "end": v(28.7, -34.88) * mm});
            skLineSegment(sketch, "E173", {"start": v(28.5, -35.63) * mm, "end": v(28.5, -36.38) * mm});
            skLineSegment(sketch, "E174", {"start": v(28.5, -36.38) * mm, "end": v(28.7, -36.38) * mm});
            skLineSegment(sketch, "E175", {"start": v(25.7, -38.43) * mm, "end": v(26.44, -38.43) * mm});
            skLineSegment(sketch, "E176", {"start": v(26.44, -38.43) * mm, "end": v(26.44, -38.62) * mm});
            skLineSegment(sketch, "E177", {"start": v(25.7, -38.43) * mm, "end": v(24.94, -38.43) * mm});
            skLineSegment(sketch, "E178", {"start": v(24.94, -38.43) * mm, "end": v(24.94, -38.62) * mm});
            skLineSegment(sketch, "E179", {"start": v(28.7, -19.62) * mm, "end": v(28.7, -20.88) * mm});
            skLineSegment(sketch, "E180", {"start": v(28.7, -22.38) * mm, "end": v(28.7, -26.48) * mm});
            skLineSegment(sketch, "E181", {"start": v(27.7, -38.62) * mm, "end": v(26.44, -38.62) * mm});
            skLineSegment(sketch, "E182", {"start": v(28.7, -37.62) * mm, "end": v(28.7, -36.38) * mm});
            skLineSegment(sketch, "E183", {"start": v(28.7, -34.88) * mm, "end": v(28.7, -30.77) * mm});
            skLineSegment(sketch, "E184", {"start": v(18.7, -13.92) * mm, "end": v(18.7, -42.92) * mm});
            skLineSegment(sketch, "E185", {"start": v(20.84, -18.62) * mm, "end": v(20.84, -20.12) * mm});
            skLineSegment(sketch, "E186", {"start": v(22.84, -20.12) * mm, "end": v(22.84, -24.12) * mm});
            skLineSegment(sketch, "E187", {"start": v(22.84, -20.12) * mm, "end": v(20.84, -20.12) * mm});
            skLineSegment(sketch, "E188", {"start": v(16.54, -18.62) * mm, "end": v(16.54, -20.12) * mm});
            skLineSegment(sketch, "E189", {"start": v(14.54, -20.12) * mm, "end": v(14.54, -24.12) * mm});
            skLineSegment(sketch, "E190", {"start": v(14.54, -20.12) * mm, "end": v(16.54, -20.12) * mm});
            skLineSegment(sketch, "E191", {"start": v(14.54, -24.12) * mm, "end": v(16.2, -24.12) * mm});
            skLineSegment(sketch, "E192", {"start": v(16.2, -24.12) * mm, "end": v(16.2, -25.42) * mm});
            skLineSegment(sketch, "E193", {"start": v(22.84, -24.12) * mm, "end": v(16.2, -25.42) * mm});
            skLineSegment(sketch, "E194", {"start": v(16.54, -38.62) * mm, "end": v(16.54, -37.12) * mm});
            skLineSegment(sketch, "E195", {"start": v(14.54, -37.12) * mm, "end": v(14.54, -33.12) * mm});
            skLineSegment(sketch, "E196", {"start": v(14.54, -37.12) * mm, "end": v(16.54, -37.12) * mm});
            skLineSegment(sketch, "E197", {"start": v(20.84, -38.62) * mm, "end": v(20.84, -37.12) * mm});
            skLineSegment(sketch, "E198", {"start": v(22.84, -37.12) * mm, "end": v(22.84, -33.12) * mm});
            skLineSegment(sketch, "E199", {"start": v(22.84, -37.12) * mm, "end": v(20.84, -37.12) * mm});
            skLineSegment(sketch, "E200", {"start": v(22.84, -33.12) * mm, "end": v(21.2, -33.12) * mm});
            skLineSegment(sketch, "E201", {"start": v(21.2, -33.12) * mm, "end": v(21.2, -31.83) * mm});
            skLineSegment(sketch, "E202", {"start": v(14.54, -33.12) * mm, "end": v(21.2, -31.83) * mm});
            skLineSegment(sketch, "E203", {"start": v(24.94, -18.62) * mm, "end": v(20.84, -18.62) * mm});
            skLineSegment(sketch, "E204", {"start": v(24.94, -38.62) * mm, "end": v(20.84, -38.62) * mm});
            skLineSegment(sketch, "E205", {"start": v(6.1, -28.62) * mm, "end": v(31.6, -28.62) * mm});
            skLineSegment(sketch, "E206", {"start": v(11.7, -17.22) * mm, "end": v(11.7, -25.12) * mm});
            skLineSegment(sketch, "E207", {"start": v(15.3, -21.63) * mm, "end": v(6.5, -21.63) * mm});
            skLineSegment(sketch, "E208", {"start": v(10.04, -20.94) * mm, "end": v(11, -19.97) * mm});
            skLineSegment(sketch, "E209", {"start": v(11, -19.97) * mm, "end": v(12.38, -19.97) * mm});
            skLineSegment(sketch, "E210", {"start": v(12.38, -19.97) * mm, "end": v(13.34, -20.94) * mm});
            skLineSegment(sketch, "E211", {"start": v(13.34, -20.94) * mm, "end": v(13.34, -22.3) * mm});
            skLineSegment(sketch, "E212", {"start": v(13.34, -22.3) * mm, "end": v(12.38, -23.28) * mm});
            skLineSegment(sketch, "E213", {"start": v(12.38, -23.28) * mm, "end": v(11, -23.28) * mm});
            skLineSegment(sketch, "E214", {"start": v(11, -23.28) * mm, "end": v(10.04, -22.3) * mm});
            skLineSegment(sketch, "E215", {"start": v(10.04, -22.3) * mm, "end": v(10.04, -20.94) * mm});
            skLineSegment(sketch, "E216", {"start": v(9.7, -18.62) * mm, "end": v(8.7, -19.62) * mm});
            skLineSegment(sketch, "E217", {"start": v(11.7, -18.83) * mm, "end": v(10.94, -18.83) * mm});
            skLineSegment(sketch, "E218", {"start": v(10.94, -18.83) * mm, "end": v(10.94, -18.62) * mm});
            skLineSegment(sketch, "E219", {"start": v(11.7, -18.83) * mm, "end": v(12.44, -18.83) * mm});
            skLineSegment(sketch, "E220", {"start": v(12.44, -18.83) * mm, "end": v(12.44, -18.62) * mm});
            skLineSegment(sketch, "E221", {"start": v(9.7, -18.62) * mm, "end": v(10.94, -18.62) * mm});
            skLineSegment(sketch, "E222", {"start": v(8.9, -21.63) * mm, "end": v(8.9, -22.38) * mm});
            skLineSegment(sketch, "E223", {"start": v(8.9, -22.38) * mm, "end": v(8.7, -22.38) * mm});
            skLineSegment(sketch, "E224", {"start": v(8.9, -21.63) * mm, "end": v(8.9, -20.88) * mm});
            skLineSegment(sketch, "E225", {"start": v(8.9, -20.88) * mm, "end": v(8.7, -20.88) * mm});
            skLineSegment(sketch, "E226", {"start": v(8.7, -19.62) * mm, "end": v(8.7, -20.88) * mm});
            skLineSegment(sketch, "E227", {"start": v(8.7, -22.38) * mm, "end": v(8.7, -26.48) * mm});
            skLineSegment(sketch, "E228", {"start": v(12.44, -18.62) * mm, "end": v(16.54, -18.62) * mm});
            skLineSegment(sketch, "E229", {"start": v(11.7, -40.02) * mm, "end": v(11.7, -32.12) * mm});
            skLineSegment(sketch, "E230", {"start": v(15.3, -35.63) * mm, "end": v(6.5, -35.63) * mm});
            skLineSegment(sketch, "E231", {"start": v(10.04, -34.94) * mm, "end": v(11, -33.98) * mm});
            skLineSegment(sketch, "E232", {"start": v(11, -33.98) * mm, "end": v(12.38, -33.98) * mm});
            skLineSegment(sketch, "E233", {"start": v(12.38, -33.98) * mm, "end": v(13.34, -34.94) * mm});
            skLineSegment(sketch, "E234", {"start": v(13.34, -34.94) * mm, "end": v(13.34, -36.3) * mm});
            skLineSegment(sketch, "E235", {"start": v(13.34, -36.3) * mm, "end": v(12.38, -37.28) * mm});
            skLineSegment(sketch, "E236", {"start": v(12.38, -37.28) * mm, "end": v(11, -37.28) * mm});
            skLineSegment(sketch, "E237", {"start": v(11, -37.28) * mm, "end": v(10.04, -36.3) * mm});
            skLineSegment(sketch, "E238", {"start": v(10.04, -36.3) * mm, "end": v(10.04, -34.94) * mm});
            skLineSegment(sketch, "E239", {"start": v(8.7, -37.62) * mm, "end": v(9.7, -38.62) * mm});
            skLineSegment(sketch, "E240", {"start": v(8.9, -35.63) * mm, "end": v(8.9, -34.88) * mm});
            skLineSegment(sketch, "E241", {"start": v(8.9, -34.88) * mm, "end": v(8.7, -34.88) * mm});
            skLineSegment(sketch, "E242", {"start": v(8.9, -35.63) * mm, "end": v(8.9, -36.38) * mm});
            skLineSegment(sketch, "E243", {"start": v(8.9, -36.38) * mm, "end": v(8.7, -36.38) * mm});
            skLineSegment(sketch, "E244", {"start": v(11.7, -38.43) * mm, "end": v(10.94, -38.43) * mm});
            skLineSegment(sketch, "E245", {"start": v(10.94, -38.43) * mm, "end": v(10.94, -38.62) * mm});
            skLineSegment(sketch, "E246", {"start": v(11.7, -38.43) * mm, "end": v(12.44, -38.43) * mm});
            skLineSegment(sketch, "E247", {"start": v(12.44, -38.43) * mm, "end": v(12.44, -38.62) * mm});
            skLineSegment(sketch, "E248", {"start": v(9.7, -38.62) * mm, "end": v(10.94, -38.62) * mm});
            skLineSegment(sketch, "E249", {"start": v(8.7, -37.62) * mm, "end": v(8.7, -36.38) * mm});
            skLineSegment(sketch, "E250", {"start": v(8.7, -34.88) * mm, "end": v(8.7, -30.77) * mm});
            skLineSegment(sketch, "E251", {"start": v(12.44, -38.62) * mm, "end": v(16.54, -38.62) * mm});
            skLineSegment(sketch, "E252", {"start": v(8.7, -26.48) * mm, "end": v(10.2, -26.48) * mm});
            skLineSegment(sketch, "E253", {"start": v(10.2, -24.48) * mm, "end": v(14.2, -24.48) * mm});
            skLineSegment(sketch, "E254", {"start": v(10.2, -24.48) * mm, "end": v(10.2, -26.48) * mm});
            skLineSegment(sketch, "E255", {"start": v(8.7, -30.77) * mm, "end": v(10.2, -30.77) * mm});
            skLineSegment(sketch, "E256", {"start": v(10.2, -32.77) * mm, "end": v(14.2, -32.77) * mm});
            skLineSegment(sketch, "E257", {"start": v(10.2, -32.77) * mm, "end": v(10.2, -30.77) * mm});
            skLineSegment(sketch, "E258", {"start": v(14.2, -32.77) * mm, "end": v(14.2, -31.12) * mm});
            skLineSegment(sketch, "E259", {"start": v(14.2, -31.12) * mm, "end": v(15.5, -31.12) * mm});
            skLineSegment(sketch, "E260", {"start": v(14.2, -24.48) * mm, "end": v(15.5, -31.12) * mm});
            skCircle(sketch, "E261", {"center": v(18.7, -28.62) * mm, "radius": 1.6 * mm});
            skSolve(sketch);
        }
        {
            var Q0;
            {var subQ9=sQuery(id+"F6.wireOp",EDGE,"E154");Q0=makeQuery(id+"F6.imprint","IMPRINT",FACE,{"disambiguationData":[TD([[makeQuery(id+"F6.imprint","IMPRINT",EDGE,{"derivedFrom":subQ9}),-1.0]])]});}
            var Q1;
            {var subQ21=sQuery(id+"F6.wireOp",EDGE,"E191");Q1=makeQuery(id+"F6.imprint","IMPRINT",FACE,{"disambiguationData":[TD([[makeQuery(id+"F6.imprint","IMPRINT",EDGE,{"derivedFrom":subQ21}),-1.0]])]});}
            var Q2;
            {var subQ1=sQuery(id+"F6.wireOp",EDGE,"E233");Q2=makeQuery(id+"F6.imprint","IMPRINT",FACE,{"disambiguationData":[TD([[makeQuery(id+"F6.imprint","IMPRINT",EDGE,{"derivedFrom":subQ1}),1.0]])]});}
            var Q3;
            {var subQ21=sQuery(id+"F6.wireOp",EDGE,"E141");Q3=makeQuery(id+"F6.imprint","IMPRINT",FACE,{"disambiguationData":[TD([[makeQuery(id+"F6.imprint","IMPRINT",EDGE,{"derivedFrom":subQ21}),-1.0]])]});}
            var Q4;
            {var subQ0=sQuery(id+"F6.wireOp",EDGE,"E205");var subQ1=sQuery(id+"F6.wireOp",EDGE,"E184");var subQ2=makeQuery(id+"F6.imprint","INTERSECT",VERTEX,{"derivedFrom":[subQ1,subQ0]});Q4=makeQuery(id+"F6.imprint","IMPRINT",FACE,{"disambiguationData":[TD([[makeQuery(id+"F6.imprint","IMPRINT",EDGE,{"disambiguationData":[TD([[subQ2,-1.0]])],"derivedFrom":subQ1}),-1.0]])]});}
            var Q5;
            {var subQ0=sQuery(id+"F6.wireOp",EDGE,"E261");var subQ1=sQuery(id+"F6.wireOp",EDGE,"E184");var subQ2=makeQuery(id+"F6.imprint","INTERSECT",VERTEX,{"disambiguationData":[OD(0.0)],"derivedFrom":[subQ1,subQ0]});Q5=makeQuery(id+"F6.imprint","IMPRINT",FACE,{"disambiguationData":[TD([[makeQuery(id+"F6.imprint","IMPRINT",EDGE,{"disambiguationData":[TD([[subQ2,-1.0]])],"derivedFrom":subQ1}),1.0]])]});}
            var Q6;
            {var subQ0=sQuery(id+"F6.wireOp",EDGE,"E261");var subQ1=sQuery(id+"F6.wireOp",EDGE,"E184");var subQ2=makeQuery(id+"F6.imprint","INTERSECT",VERTEX,{"disambiguationData":[OD(0.0)],"derivedFrom":[subQ1,subQ0]});Q6=makeQuery(id+"F6.imprint","IMPRINT",FACE,{"disambiguationData":[TD([[makeQuery(id+"F6.imprint","IMPRINT",EDGE,{"disambiguationData":[TD([[subQ2,-1.0]])],"derivedFrom":subQ1}),-1.0]])]});}
            var Q7;
            {var subQ0=sQuery(id+"F6.wireOp",EDGE,"E205");var subQ1=sQuery(id+"F6.wireOp",EDGE,"E184");var subQ2=makeQuery(id+"F6.imprint","INTERSECT",VERTEX,{"derivedFrom":[subQ1,subQ0]});Q7=makeQuery(id+"F6.imprint","IMPRINT",FACE,{"disambiguationData":[TD([[makeQuery(id+"F6.imprint","IMPRINT",EDGE,{"disambiguationData":[TD([[subQ2,-1.0]])],"derivedFrom":subQ1}),1.0]])]});}
            var Q8;
            Q8=makeQuery(id+"F6.imprint","IMPRINT",FACE,{"disambiguationData":[TD([[makeQuery(id+"F6.imprint","IMPRINT",EDGE,{"derivedFrom":sQuery(id+"F6.wireOp",EDGE,"E188")}),-1.0]])]});
            var Q9;
            {var subQ3=sQuery(id+"F6.wireOp",EDGE,"E146");Q9=makeQuery(id+"F6.imprint","IMPRINT",FACE,{"disambiguationData":[TD([[makeQuery(id+"F6.imprint","IMPRINT",EDGE,{"derivedFrom":subQ3}),-1.0]])]});}
            var Q10;
            {var subQ0=sQuery(id+"F6.wireOp",EDGE,"E214");Q10=makeQuery(id+"F6.imprint","IMPRINT",FACE,{"disambiguationData":[TD([[makeQuery(id+"F6.imprint","IMPRINT",EDGE,{"derivedFrom":subQ0}),-1.0]])]});}
            var Q11;
            {var subQ8=sQuery(id+"F6.wireOp",EDGE,"E231");Q11=makeQuery(id+"F6.imprint","IMPRINT",FACE,{"disambiguationData":[TD([[makeQuery(id+"F6.imprint","IMPRINT",EDGE,{"derivedFrom":subQ8}),1.0]])]});}
            var Q12;
            {var subQ8=sQuery(id+"F6.wireOp",EDGE,"E214");Q12=makeQuery(id+"F6.imprint","IMPRINT",FACE,{"disambiguationData":[TD([[makeQuery(id+"F6.imprint","IMPRINT",EDGE,{"derivedFrom":subQ8}),1.0]])]});}
            var Q13;
            Q13=makeQuery(id+"F6.imprint","IMPRINT",FACE,{"disambiguationData":[TD([[makeQuery(id+"F6.imprint","IMPRINT",EDGE,{"derivedFrom":sQuery(id+"F6.wireOp",EDGE,"E194")}),1.0]])]});
            var Q14;
            Q14=makeQuery(id+"F6.imprint","IMPRINT",FACE,{"disambiguationData":[TD([[makeQuery(id+"F6.imprint","IMPRINT",EDGE,{"derivedFrom":sQuery(id+"F6.wireOp",EDGE,"E135")}),1.0]])]});
            var Q15;
            {var subQ0=sQuery(id+"F6.wireOp",EDGE,"E146");Q15=makeQuery(id+"F6.imprint","IMPRINT",FACE,{"disambiguationData":[TD([[makeQuery(id+"F6.imprint","IMPRINT",EDGE,{"derivedFrom":subQ0}),1.0]])]});}
            var Q16;
            {var subQ1=sQuery(id+"F6.wireOp",EDGE,"E144");Q16=makeQuery(id+"F6.imprint","IMPRINT",FACE,{"disambiguationData":[TD([[makeQuery(id+"F6.imprint","IMPRINT",EDGE,{"derivedFrom":subQ1}),1.0]])]});}
            var Q17;
            {var subQ5=sQuery(id+"F6.wireOp",EDGE,"E156");Q17=makeQuery(id+"F6.imprint","IMPRINT",FACE,{"disambiguationData":[TD([[makeQuery(id+"F6.imprint","IMPRINT",EDGE,{"derivedFrom":subQ5}),-1.0]])]});}
            var Q18;
            {var subQ0=sQuery(id+"F6.wireOp",EDGE,"E233");Q18=makeQuery(id+"F6.imprint","IMPRINT",FACE,{"disambiguationData":[TD([[makeQuery(id+"F6.imprint","IMPRINT",EDGE,{"derivedFrom":subQ0}),-1.0]])]});}
            var Q19;
            {var subQ1=sQuery(id+"F6.wireOp",EDGE,"E208");Q19=makeQuery(id+"F6.imprint","IMPRINT",FACE,{"disambiguationData":[TD([[makeQuery(id+"F6.imprint","IMPRINT",EDGE,{"derivedFrom":subQ1}),-1.0]])]});}
            var Q20;
            {var subQ0=sQuery(id+"F6.wireOp",EDGE,"E212");Q20=makeQuery(id+"F6.imprint","IMPRINT",FACE,{"disambiguationData":[TD([[makeQuery(id+"F6.imprint","IMPRINT",EDGE,{"derivedFrom":subQ0}),-1.0]])]});}
            var Q21;
            {var subQ8=sQuery(id+"F6.wireOp",EDGE,"E208");Q21=makeQuery(id+"F6.imprint","IMPRINT",FACE,{"disambiguationData":[TD([[makeQuery(id+"F6.imprint","IMPRINT",EDGE,{"derivedFrom":subQ8}),1.0]])]});}
            var Q22;
            {var subQ0=sQuery(id+"F6.wireOp",EDGE,"E210");Q22=makeQuery(id+"F6.imprint","IMPRINT",FACE,{"disambiguationData":[TD([[makeQuery(id+"F6.imprint","IMPRINT",EDGE,{"derivedFrom":subQ0}),-1.0]])]});}
            var Q23;
            {var subQ0=sQuery(id+"F6.wireOp",EDGE,"E148");Q23=makeQuery(id+"F6.imprint","IMPRINT",FACE,{"disambiguationData":[TD([[makeQuery(id+"F6.imprint","IMPRINT",EDGE,{"derivedFrom":subQ0}),1.0]])]});}
            var Q24;
            {var subQ0=sQuery(id+"F6.wireOp",EDGE,"E150");Q24=makeQuery(id+"F6.imprint","IMPRINT",FACE,{"disambiguationData":[TD([[makeQuery(id+"F6.imprint","IMPRINT",EDGE,{"derivedFrom":subQ0}),1.0]])]});}
            var Q25;
            Q25=makeQuery(id+"F6.imprint","IMPRINT",FACE,{"disambiguationData":[TD([[makeQuery(id+"F6.imprint","IMPRINT",EDGE,{"derivedFrom":sQuery(id+"F6.wireOp",EDGE,"E138")}),-1.0]])]});
            var Q26;
            {var subQ0=sQuery(id+"F6.wireOp",EDGE,"E156");Q26=makeQuery(id+"F6.imprint","IMPRINT",FACE,{"disambiguationData":[TD([[makeQuery(id+"F6.imprint","IMPRINT",EDGE,{"derivedFrom":subQ0}),1.0]])]});}
            var Q27;
            {var subQ0=sQuery(id+"F6.wireOp",EDGE,"E158");Q27=makeQuery(id+"F6.imprint","IMPRINT",FACE,{"disambiguationData":[TD([[makeQuery(id+"F6.imprint","IMPRINT",EDGE,{"derivedFrom":subQ0}),1.0]])]});}
            var Q28;
            {var subQ0=sQuery(id+"F6.wireOp",EDGE,"E154");Q28=makeQuery(id+"F6.imprint","IMPRINT",FACE,{"disambiguationData":[TD([[makeQuery(id+"F6.imprint","IMPRINT",EDGE,{"derivedFrom":subQ0}),1.0]])]});}
            var Q29;
            {var subQ1=sQuery(id+"F6.wireOp",EDGE,"E152");Q29=makeQuery(id+"F6.imprint","IMPRINT",FACE,{"disambiguationData":[TD([[makeQuery(id+"F6.imprint","IMPRINT",EDGE,{"derivedFrom":subQ1}),1.0]])]});}
            var Q30;
            {var subQ6=sQuery(id+"F6.wireOp",EDGE,"E237");Q30=makeQuery(id+"F6.imprint","IMPRINT",FACE,{"disambiguationData":[TD([[makeQuery(id+"F6.imprint","IMPRINT",EDGE,{"derivedFrom":subQ6}),1.0]])]});}
            var Q31;
            {var subQ0=sQuery(id+"F6.wireOp",EDGE,"E235");Q31=makeQuery(id+"F6.imprint","IMPRINT",FACE,{"disambiguationData":[TD([[makeQuery(id+"F6.imprint","IMPRINT",EDGE,{"derivedFrom":subQ0}),-1.0]])]});}
            var Q32;
            {var subQ1=sQuery(id+"F6.wireOp",EDGE,"E231");Q32=makeQuery(id+"F6.imprint","IMPRINT",FACE,{"disambiguationData":[TD([[makeQuery(id+"F6.imprint","IMPRINT",EDGE,{"derivedFrom":subQ1}),-1.0]])]});}
            var Q33;
            {var subQ0=sQuery(id+"F6.wireOp",EDGE,"E237");Q33=makeQuery(id+"F6.imprint","IMPRINT",FACE,{"disambiguationData":[TD([[makeQuery(id+"F6.imprint","IMPRINT",EDGE,{"derivedFrom":subQ0}),-1.0]])]});}
            var Q34;
            {var subQ2=sQuery(id+"F6.wireOp",EDGE,"E144");Q34=makeQuery(id+"F6.imprint","IMPRINT",FACE,{"disambiguationData":[TD([[makeQuery(id+"F6.imprint","IMPRINT",EDGE,{"derivedFrom":subQ2}),-1.0]])]});}
            var Q35;
            {var subQ3=sQuery(id+"F6.wireOp",EDGE,"E158");Q35=makeQuery(id+"F6.imprint","IMPRINT",FACE,{"disambiguationData":[TD([[makeQuery(id+"F6.imprint","IMPRINT",EDGE,{"derivedFrom":subQ3}),-1.0]])]});}
            extrude(context, id + "F7", {"entities" : qUnion([Q0, Q1, Q2, Q3, Q4, Q5, Q6, Q7, Q8, Q9, Q10, Q11, Q12, Q13, Q14, Q15, Q16, Q17, Q18, Q19, Q20, Q21, Q22, Q23, Q24, Q25, Q26, Q27, Q28, Q29, Q30, Q31, Q32, Q33, Q34, Q35]), "depth" : 630 * mm, "offsetDistance" : 25 * mm});
        }
        {
            var Q0;
            Q0=makeQuery(id+"F7.opExtrude","SWEPT_BODY",BODY,{"disambiguationData":[OSD([sQuery(id+"F6.wireOp",EDGE,"E135"),sQuery(id+"F6.wireOp",EDGE,"E136"),sQuery(id+"F6.wireOp",EDGE,"E137"),sQuery(id+"F6.wireOp",EDGE,"E138"),sQuery(id+"F6.wireOp",EDGE,"E139"),sQuery(id+"F6.wireOp",EDGE,"E140"),sQuery(id+"F6.wireOp",EDGE,"E141"),sQuery(id+"F6.wireOp",EDGE,"E142"),sQuery(id+"F6.wireOp",EDGE,"E143"),sQuery(id+"F6.wireOp",EDGE,"E160"),sQuery(id+"F6.wireOp",EDGE,"E161"),sQuery(id+"F6.wireOp",EDGE,"E162"),sQuery(id+"F6.wireOp",EDGE,"E163"),sQuery(id+"F6.wireOp",EDGE,"E164"),sQuery(id+"F6.wireOp",EDGE,"E165"),sQuery(id+"F6.wireOp",EDGE,"E166"),sQuery(id+"F6.wireOp",EDGE,"E167"),sQuery(id+"F6.wireOp",EDGE,"E168"),sQuery(id+"F6.wireOp",EDGE,"E169"),sQuery(id+"F6.wireOp",EDGE,"E170"),sQuery(id+"F6.wireOp",EDGE,"E171"),sQuery(id+"F6.wireOp",EDGE,"E172"),sQuery(id+"F6.wireOp",EDGE,"E173"),sQuery(id+"F6.wireOp",EDGE,"E174"),sQuery(id+"F6.wireOp",EDGE,"E175"),sQuery(id+"F6.wireOp",EDGE,"E176"),sQuery(id+"F6.wireOp",EDGE,"E177"),sQuery(id+"F6.wireOp",EDGE,"E178"),sQuery(id+"F6.wireOp",EDGE,"E179"),sQuery(id+"F6.wireOp",EDGE,"E180"),sQuery(id+"F6.wireOp",EDGE,"E181"),sQuery(id+"F6.wireOp",EDGE,"E182"),sQuery(id+"F6.wireOp",EDGE,"E183"),sQuery(id+"F6.wireOp",EDGE,"E185"),sQuery(id+"F6.wireOp",EDGE,"E186"),sQuery(id+"F6.wireOp",EDGE,"E187"),sQuery(id+"F6.wireOp",EDGE,"E188"),sQuery(id+"F6.wireOp",EDGE,"E189"),sQuery(id+"F6.wireOp",EDGE,"E190"),sQuery(id+"F6.wireOp",EDGE,"E191"),sQuery(id+"F6.wireOp",EDGE,"E192"),sQuery(id+"F6.wireOp",EDGE,"E193"),sQuery(id+"F6.wireOp",EDGE,"E194"),sQuery(id+"F6.wireOp",EDGE,"E195"),sQuery(id+"F6.wireOp",EDGE,"E196"),sQuery(id+"F6.wireOp",EDGE,"E197"),sQuery(id+"F6.wireOp",EDGE,"E198"),sQuery(id+"F6.wireOp",EDGE,"E199"),sQuery(id+"F6.wireOp",EDGE,"E200"),sQuery(id+"F6.wireOp",EDGE,"E201"),sQuery(id+"F6.wireOp",EDGE,"E202"),sQuery(id+"F6.wireOp",EDGE,"E203"),sQuery(id+"F6.wireOp",EDGE,"E204"),sQuery(id+"F6.wireOp",EDGE,"E216"),sQuery(id+"F6.wireOp",EDGE,"E217"),sQuery(id+"F6.wireOp",EDGE,"E218"),sQuery(id+"F6.wireOp",EDGE,"E219"),sQuery(id+"F6.wireOp",EDGE,"E220"),sQuery(id+"F6.wireOp",EDGE,"E221"),sQuery(id+"F6.wireOp",EDGE,"E222"),sQuery(id+"F6.wireOp",EDGE,"E223"),sQuery(id+"F6.wireOp",EDGE,"E224"),sQuery(id+"F6.wireOp",EDGE,"E225"),sQuery(id+"F6.wireOp",EDGE,"E226"),sQuery(id+"F6.wireOp",EDGE,"E227"),sQuery(id+"F6.wireOp",EDGE,"E228"),sQuery(id+"F6.wireOp",EDGE,"E239"),sQuery(id+"F6.wireOp",EDGE,"E240"),sQuery(id+"F6.wireOp",EDGE,"E241"),sQuery(id+"F6.wireOp",EDGE,"E242"),sQuery(id+"F6.wireOp",EDGE,"E243"),sQuery(id+"F6.wireOp",EDGE,"E244"),sQuery(id+"F6.wireOp",EDGE,"E245"),sQuery(id+"F6.wireOp",EDGE,"E246"),sQuery(id+"F6.wireOp",EDGE,"E247"),sQuery(id+"F6.wireOp",EDGE,"E248"),sQuery(id+"F6.wireOp",EDGE,"E249"),sQuery(id+"F6.wireOp",EDGE,"E250"),sQuery(id+"F6.wireOp",EDGE,"E251"),sQuery(id+"F6.wireOp",EDGE,"E252"),sQuery(id+"F6.wireOp",EDGE,"E253"),sQuery(id+"F6.wireOp",EDGE,"E254"),sQuery(id+"F6.wireOp",EDGE,"E255"),sQuery(id+"F6.wireOp",EDGE,"E256"),sQuery(id+"F6.wireOp",EDGE,"E257"),sQuery(id+"F6.wireOp",EDGE,"E258"),sQuery(id+"F6.wireOp",EDGE,"E259"),sQuery(id+"F6.wireOp",EDGE,"E260")])]});
            transform(context, id + "F8", {"entities" : qUnion([Q0]), "transformType" : TransformType.TRANSLATION_3D, "dx" : -28.7 * mm, "dy" : 0 * mm, "dz" : 0 * mm, "makeCopy" : false});
        }
        {
            var Q0;
            Q0=makeQuery(id+"F7.opExtrude","SWEPT_BODY",BODY,{"disambiguationData":[OSD([sQuery(id+"F6.wireOp",EDGE,"E135"),sQuery(id+"F6.wireOp",EDGE,"E136"),sQuery(id+"F6.wireOp",EDGE,"E137"),sQuery(id+"F6.wireOp",EDGE,"E138"),sQuery(id+"F6.wireOp",EDGE,"E139"),sQuery(id+"F6.wireOp",EDGE,"E140"),sQuery(id+"F6.wireOp",EDGE,"E141"),sQuery(id+"F6.wireOp",EDGE,"E142"),sQuery(id+"F6.wireOp",EDGE,"E143"),sQuery(id+"F6.wireOp",EDGE,"E160"),sQuery(id+"F6.wireOp",EDGE,"E161"),sQuery(id+"F6.wireOp",EDGE,"E162"),sQuery(id+"F6.wireOp",EDGE,"E163"),sQuery(id+"F6.wireOp",EDGE,"E164"),sQuery(id+"F6.wireOp",EDGE,"E165"),sQuery(id+"F6.wireOp",EDGE,"E166"),sQuery(id+"F6.wireOp",EDGE,"E167"),sQuery(id+"F6.wireOp",EDGE,"E168"),sQuery(id+"F6.wireOp",EDGE,"E169"),sQuery(id+"F6.wireOp",EDGE,"E170"),sQuery(id+"F6.wireOp",EDGE,"E171"),sQuery(id+"F6.wireOp",EDGE,"E172"),sQuery(id+"F6.wireOp",EDGE,"E173"),sQuery(id+"F6.wireOp",EDGE,"E174"),sQuery(id+"F6.wireOp",EDGE,"E175"),sQuery(id+"F6.wireOp",EDGE,"E176"),sQuery(id+"F6.wireOp",EDGE,"E177"),sQuery(id+"F6.wireOp",EDGE,"E178"),sQuery(id+"F6.wireOp",EDGE,"E179"),sQuery(id+"F6.wireOp",EDGE,"E180"),sQuery(id+"F6.wireOp",EDGE,"E181"),sQuery(id+"F6.wireOp",EDGE,"E182"),sQuery(id+"F6.wireOp",EDGE,"E183"),sQuery(id+"F6.wireOp",EDGE,"E185"),sQuery(id+"F6.wireOp",EDGE,"E186"),sQuery(id+"F6.wireOp",EDGE,"E187"),sQuery(id+"F6.wireOp",EDGE,"E188"),sQuery(id+"F6.wireOp",EDGE,"E189"),sQuery(id+"F6.wireOp",EDGE,"E190"),sQuery(id+"F6.wireOp",EDGE,"E191"),sQuery(id+"F6.wireOp",EDGE,"E192"),sQuery(id+"F6.wireOp",EDGE,"E193"),sQuery(id+"F6.wireOp",EDGE,"E194"),sQuery(id+"F6.wireOp",EDGE,"E195"),sQuery(id+"F6.wireOp",EDGE,"E196"),sQuery(id+"F6.wireOp",EDGE,"E197"),sQuery(id+"F6.wireOp",EDGE,"E198"),sQuery(id+"F6.wireOp",EDGE,"E199"),sQuery(id+"F6.wireOp",EDGE,"E200"),sQuery(id+"F6.wireOp",EDGE,"E201"),sQuery(id+"F6.wireOp",EDGE,"E202"),sQuery(id+"F6.wireOp",EDGE,"E203"),sQuery(id+"F6.wireOp",EDGE,"E204"),sQuery(id+"F6.wireOp",EDGE,"E216"),sQuery(id+"F6.wireOp",EDGE,"E217"),sQuery(id+"F6.wireOp",EDGE,"E218"),sQuery(id+"F6.wireOp",EDGE,"E219"),sQuery(id+"F6.wireOp",EDGE,"E220"),sQuery(id+"F6.wireOp",EDGE,"E221"),sQuery(id+"F6.wireOp",EDGE,"E222"),sQuery(id+"F6.wireOp",EDGE,"E223"),sQuery(id+"F6.wireOp",EDGE,"E224"),sQuery(id+"F6.wireOp",EDGE,"E225"),sQuery(id+"F6.wireOp",EDGE,"E226"),sQuery(id+"F6.wireOp",EDGE,"E227"),sQuery(id+"F6.wireOp",EDGE,"E228"),sQuery(id+"F6.wireOp",EDGE,"E239"),sQuery(id+"F6.wireOp",EDGE,"E240"),sQuery(id+"F6.wireOp",EDGE,"E241"),sQuery(id+"F6.wireOp",EDGE,"E242"),sQuery(id+"F6.wireOp",EDGE,"E243"),sQuery(id+"F6.wireOp",EDGE,"E244"),sQuery(id+"F6.wireOp",EDGE,"E245"),sQuery(id+"F6.wireOp",EDGE,"E246"),sQuery(id+"F6.wireOp",EDGE,"E247"),sQuery(id+"F6.wireOp",EDGE,"E248"),sQuery(id+"F6.wireOp",EDGE,"E249"),sQuery(id+"F6.wireOp",EDGE,"E250"),sQuery(id+"F6.wireOp",EDGE,"E251"),sQuery(id+"F6.wireOp",EDGE,"E252"),sQuery(id+"F6.wireOp",EDGE,"E253"),sQuery(id+"F6.wireOp",EDGE,"E254"),sQuery(id+"F6.wireOp",EDGE,"E255"),sQuery(id+"F6.wireOp",EDGE,"E256"),sQuery(id+"F6.wireOp",EDGE,"E257"),sQuery(id+"F6.wireOp",EDGE,"E258"),sQuery(id+"F6.wireOp",EDGE,"E259"),sQuery(id+"F6.wireOp",EDGE,"E260")])]});
            transform(context, id + "F9", {"entities" : qUnion([Q0]), "transformType" : TransformType.TRANSLATION_3D, "dx" : 0 * mm, "dy" : 0 * mm, "dz" : 480 * mm, "makeCopy" : true});
        }
        {
            var Q0;
            Q0=makeQuery(id+"F9.opPattern","COPY",BODY,{"derivedFrom":makeQuery(id+"F7.opExtrude","SWEPT_BODY",BODY,{"disambiguationData":[OSD([sQuery(id+"F6.wireOp",EDGE,"E135"),sQuery(id+"F6.wireOp",EDGE,"E136"),sQuery(id+"F6.wireOp",EDGE,"E137"),sQuery(id+"F6.wireOp",EDGE,"E138"),sQuery(id+"F6.wireOp",EDGE,"E139"),sQuery(id+"F6.wireOp",EDGE,"E140"),sQuery(id+"F6.wireOp",EDGE,"E141"),sQuery(id+"F6.wireOp",EDGE,"E142"),sQuery(id+"F6.wireOp",EDGE,"E143"),sQuery(id+"F6.wireOp",EDGE,"E160"),sQuery(id+"F6.wireOp",EDGE,"E161"),sQuery(id+"F6.wireOp",EDGE,"E162"),sQuery(id+"F6.wireOp",EDGE,"E163"),sQuery(id+"F6.wireOp",EDGE,"E164"),sQuery(id+"F6.wireOp",EDGE,"E165"),sQuery(id+"F6.wireOp",EDGE,"E166"),sQuery(id+"F6.wireOp",EDGE,"E167"),sQuery(id+"F6.wireOp",EDGE,"E168"),sQuery(id+"F6.wireOp",EDGE,"E169"),sQuery(id+"F6.wireOp",EDGE,"E170"),sQuery(id+"F6.wireOp",EDGE,"E171"),sQuery(id+"F6.wireOp",EDGE,"E172"),sQuery(id+"F6.wireOp",EDGE,"E173"),sQuery(id+"F6.wireOp",EDGE,"E174"),sQuery(id+"F6.wireOp",EDGE,"E175"),sQuery(id+"F6.wireOp",EDGE,"E176"),sQuery(id+"F6.wireOp",EDGE,"E177"),sQuery(id+"F6.wireOp",EDGE,"E178"),sQuery(id+"F6.wireOp",EDGE,"E179"),sQuery(id+"F6.wireOp",EDGE,"E180"),sQuery(id+"F6.wireOp",EDGE,"E181"),sQuery(id+"F6.wireOp",EDGE,"E182"),sQuery(id+"F6.wireOp",EDGE,"E183"),sQuery(id+"F6.wireOp",EDGE,"E185"),sQuery(id+"F6.wireOp",EDGE,"E186"),sQuery(id+"F6.wireOp",EDGE,"E187"),sQuery(id+"F6.wireOp",EDGE,"E188"),sQuery(id+"F6.wireOp",EDGE,"E189"),sQuery(id+"F6.wireOp",EDGE,"E190"),sQuery(id+"F6.wireOp",EDGE,"E191"),sQuery(id+"F6.wireOp",EDGE,"E192"),sQuery(id+"F6.wireOp",EDGE,"E193"),sQuery(id+"F6.wireOp",EDGE,"E194"),sQuery(id+"F6.wireOp",EDGE,"E195"),sQuery(id+"F6.wireOp",EDGE,"E196"),sQuery(id+"F6.wireOp",EDGE,"E197"),sQuery(id+"F6.wireOp",EDGE,"E198"),sQuery(id+"F6.wireOp",EDGE,"E199"),sQuery(id+"F6.wireOp",EDGE,"E200"),sQuery(id+"F6.wireOp",EDGE,"E201"),sQuery(id+"F6.wireOp",EDGE,"E202"),sQuery(id+"F6.wireOp",EDGE,"E203"),sQuery(id+"F6.wireOp",EDGE,"E204"),sQuery(id+"F6.wireOp",EDGE,"E216"),sQuery(id+"F6.wireOp",EDGE,"E217"),sQuery(id+"F6.wireOp",EDGE,"E218"),sQuery(id+"F6.wireOp",EDGE,"E219"),sQuery(id+"F6.wireOp",EDGE,"E220"),sQuery(id+"F6.wireOp",EDGE,"E221"),sQuery(id+"F6.wireOp",EDGE,"E222"),sQuery(id+"F6.wireOp",EDGE,"E223"),sQuery(id+"F6.wireOp",EDGE,"E224"),sQuery(id+"F6.wireOp",EDGE,"E225"),sQuery(id+"F6.wireOp",EDGE,"E226"),sQuery(id+"F6.wireOp",EDGE,"E227"),sQuery(id+"F6.wireOp",EDGE,"E228"),sQuery(id+"F6.wireOp",EDGE,"E239"),sQuery(id+"F6.wireOp",EDGE,"E240"),sQuery(id+"F6.wireOp",EDGE,"E241"),sQuery(id+"F6.wireOp",EDGE,"E242"),sQuery(id+"F6.wireOp",EDGE,"E243"),sQuery(id+"F6.wireOp",EDGE,"E244"),sQuery(id+"F6.wireOp",EDGE,"E245"),sQuery(id+"F6.wireOp",EDGE,"E246"),sQuery(id+"F6.wireOp",EDGE,"E247"),sQuery(id+"F6.wireOp",EDGE,"E248"),sQuery(id+"F6.wireOp",EDGE,"E249"),sQuery(id+"F6.wireOp",EDGE,"E250"),sQuery(id+"F6.wireOp",EDGE,"E251"),sQuery(id+"F6.wireOp",EDGE,"E252"),sQuery(id+"F6.wireOp",EDGE,"E253"),sQuery(id+"F6.wireOp",EDGE,"E254"),sQuery(id+"F6.wireOp",EDGE,"E255"),sQuery(id+"F6.wireOp",EDGE,"E256"),sQuery(id+"F6.wireOp",EDGE,"E257"),sQuery(id+"F6.wireOp",EDGE,"E258"),sQuery(id+"F6.wireOp",EDGE,"E259"),sQuery(id+"F6.wireOp",EDGE,"E260")])]}),"instanceName":"1"});
            var Q1;
            Q1=makeQuery(id+"F7.opExtrude","SWEPT_BODY",BODY,{"disambiguationData":[OSD([sQuery(id+"F6.wireOp",EDGE,"E135"),sQuery(id+"F6.wireOp",EDGE,"E136"),sQuery(id+"F6.wireOp",EDGE,"E137"),sQuery(id+"F6.wireOp",EDGE,"E138"),sQuery(id+"F6.wireOp",EDGE,"E139"),sQuery(id+"F6.wireOp",EDGE,"E140"),sQuery(id+"F6.wireOp",EDGE,"E141"),sQuery(id+"F6.wireOp",EDGE,"E142"),sQuery(id+"F6.wireOp",EDGE,"E143"),sQuery(id+"F6.wireOp",EDGE,"E160"),sQuery(id+"F6.wireOp",EDGE,"E161"),sQuery(id+"F6.wireOp",EDGE,"E162"),sQuery(id+"F6.wireOp",EDGE,"E163"),sQuery(id+"F6.wireOp",EDGE,"E164"),sQuery(id+"F6.wireOp",EDGE,"E165"),sQuery(id+"F6.wireOp",EDGE,"E166"),sQuery(id+"F6.wireOp",EDGE,"E167"),sQuery(id+"F6.wireOp",EDGE,"E168"),sQuery(id+"F6.wireOp",EDGE,"E169"),sQuery(id+"F6.wireOp",EDGE,"E170"),sQuery(id+"F6.wireOp",EDGE,"E171"),sQuery(id+"F6.wireOp",EDGE,"E172"),sQuery(id+"F6.wireOp",EDGE,"E173"),sQuery(id+"F6.wireOp",EDGE,"E174"),sQuery(id+"F6.wireOp",EDGE,"E175"),sQuery(id+"F6.wireOp",EDGE,"E176"),sQuery(id+"F6.wireOp",EDGE,"E177"),sQuery(id+"F6.wireOp",EDGE,"E178"),sQuery(id+"F6.wireOp",EDGE,"E179"),sQuery(id+"F6.wireOp",EDGE,"E180"),sQuery(id+"F6.wireOp",EDGE,"E181"),sQuery(id+"F6.wireOp",EDGE,"E182"),sQuery(id+"F6.wireOp",EDGE,"E183"),sQuery(id+"F6.wireOp",EDGE,"E185"),sQuery(id+"F6.wireOp",EDGE,"E186"),sQuery(id+"F6.wireOp",EDGE,"E187"),sQuery(id+"F6.wireOp",EDGE,"E188"),sQuery(id+"F6.wireOp",EDGE,"E189"),sQuery(id+"F6.wireOp",EDGE,"E190"),sQuery(id+"F6.wireOp",EDGE,"E191"),sQuery(id+"F6.wireOp",EDGE,"E192"),sQuery(id+"F6.wireOp",EDGE,"E193"),sQuery(id+"F6.wireOp",EDGE,"E194"),sQuery(id+"F6.wireOp",EDGE,"E195"),sQuery(id+"F6.wireOp",EDGE,"E196"),sQuery(id+"F6.wireOp",EDGE,"E197"),sQuery(id+"F6.wireOp",EDGE,"E198"),sQuery(id+"F6.wireOp",EDGE,"E199"),sQuery(id+"F6.wireOp",EDGE,"E200"),sQuery(id+"F6.wireOp",EDGE,"E201"),sQuery(id+"F6.wireOp",EDGE,"E202"),sQuery(id+"F6.wireOp",EDGE,"E203"),sQuery(id+"F6.wireOp",EDGE,"E204"),sQuery(id+"F6.wireOp",EDGE,"E216"),sQuery(id+"F6.wireOp",EDGE,"E217"),sQuery(id+"F6.wireOp",EDGE,"E218"),sQuery(id+"F6.wireOp",EDGE,"E219"),sQuery(id+"F6.wireOp",EDGE,"E220"),sQuery(id+"F6.wireOp",EDGE,"E221"),sQuery(id+"F6.wireOp",EDGE,"E222"),sQuery(id+"F6.wireOp",EDGE,"E223"),sQuery(id+"F6.wireOp",EDGE,"E224"),sQuery(id+"F6.wireOp",EDGE,"E225"),sQuery(id+"F6.wireOp",EDGE,"E226"),sQuery(id+"F6.wireOp",EDGE,"E227"),sQuery(id+"F6.wireOp",EDGE,"E228"),sQuery(id+"F6.wireOp",EDGE,"E239"),sQuery(id+"F6.wireOp",EDGE,"E240"),sQuery(id+"F6.wireOp",EDGE,"E241"),sQuery(id+"F6.wireOp",EDGE,"E242"),sQuery(id+"F6.wireOp",EDGE,"E243"),sQuery(id+"F6.wireOp",EDGE,"E244"),sQuery(id+"F6.wireOp",EDGE,"E245"),sQuery(id+"F6.wireOp",EDGE,"E246"),sQuery(id+"F6.wireOp",EDGE,"E247"),sQuery(id+"F6.wireOp",EDGE,"E248"),sQuery(id+"F6.wireOp",EDGE,"E249"),sQuery(id+"F6.wireOp",EDGE,"E250"),sQuery(id+"F6.wireOp",EDGE,"E251"),sQuery(id+"F6.wireOp",EDGE,"E252"),sQuery(id+"F6.wireOp",EDGE,"E253"),sQuery(id+"F6.wireOp",EDGE,"E254"),sQuery(id+"F6.wireOp",EDGE,"E255"),sQuery(id+"F6.wireOp",EDGE,"E256"),sQuery(id+"F6.wireOp",EDGE,"E257"),sQuery(id+"F6.wireOp",EDGE,"E258"),sQuery(id+"F6.wireOp",EDGE,"E259"),sQuery(id+"F6.wireOp",EDGE,"E260")])]});
            transform(context, id + "F10", {"entities" : qUnion([Q0, Q1]), "transformType" : TransformType.TRANSLATION_3D, "dx" : -750 * mm, "dy" : 0 * mm, "dz" : 0 * mm, "makeCopy" : true});
        }
        {
            var Q0;
            Q0=makeQuery(id+"F7.opExtrude","SWEPT_BODY",BODY,{"disambiguationData":[OSD([sQuery(id+"F6.wireOp",EDGE,"E135"),sQuery(id+"F6.wireOp",EDGE,"E136"),sQuery(id+"F6.wireOp",EDGE,"E137"),sQuery(id+"F6.wireOp",EDGE,"E138"),sQuery(id+"F6.wireOp",EDGE,"E139"),sQuery(id+"F6.wireOp",EDGE,"E140"),sQuery(id+"F6.wireOp",EDGE,"E141"),sQuery(id+"F6.wireOp",EDGE,"E142"),sQuery(id+"F6.wireOp",EDGE,"E143"),sQuery(id+"F6.wireOp",EDGE,"E160"),sQuery(id+"F6.wireOp",EDGE,"E161"),sQuery(id+"F6.wireOp",EDGE,"E162"),sQuery(id+"F6.wireOp",EDGE,"E163"),sQuery(id+"F6.wireOp",EDGE,"E164"),sQuery(id+"F6.wireOp",EDGE,"E165"),sQuery(id+"F6.wireOp",EDGE,"E166"),sQuery(id+"F6.wireOp",EDGE,"E167"),sQuery(id+"F6.wireOp",EDGE,"E168"),sQuery(id+"F6.wireOp",EDGE,"E169"),sQuery(id+"F6.wireOp",EDGE,"E170"),sQuery(id+"F6.wireOp",EDGE,"E171"),sQuery(id+"F6.wireOp",EDGE,"E172"),sQuery(id+"F6.wireOp",EDGE,"E173"),sQuery(id+"F6.wireOp",EDGE,"E174"),sQuery(id+"F6.wireOp",EDGE,"E175"),sQuery(id+"F6.wireOp",EDGE,"E176"),sQuery(id+"F6.wireOp",EDGE,"E177"),sQuery(id+"F6.wireOp",EDGE,"E178"),sQuery(id+"F6.wireOp",EDGE,"E179"),sQuery(id+"F6.wireOp",EDGE,"E180"),sQuery(id+"F6.wireOp",EDGE,"E181"),sQuery(id+"F6.wireOp",EDGE,"E182"),sQuery(id+"F6.wireOp",EDGE,"E183"),sQuery(id+"F6.wireOp",EDGE,"E185"),sQuery(id+"F6.wireOp",EDGE,"E186"),sQuery(id+"F6.wireOp",EDGE,"E187"),sQuery(id+"F6.wireOp",EDGE,"E188"),sQuery(id+"F6.wireOp",EDGE,"E189"),sQuery(id+"F6.wireOp",EDGE,"E190"),sQuery(id+"F6.wireOp",EDGE,"E191"),sQuery(id+"F6.wireOp",EDGE,"E192"),sQuery(id+"F6.wireOp",EDGE,"E193"),sQuery(id+"F6.wireOp",EDGE,"E194"),sQuery(id+"F6.wireOp",EDGE,"E195"),sQuery(id+"F6.wireOp",EDGE,"E196"),sQuery(id+"F6.wireOp",EDGE,"E197"),sQuery(id+"F6.wireOp",EDGE,"E198"),sQuery(id+"F6.wireOp",EDGE,"E199"),sQuery(id+"F6.wireOp",EDGE,"E200"),sQuery(id+"F6.wireOp",EDGE,"E201"),sQuery(id+"F6.wireOp",EDGE,"E202"),sQuery(id+"F6.wireOp",EDGE,"E203"),sQuery(id+"F6.wireOp",EDGE,"E204"),sQuery(id+"F6.wireOp",EDGE,"E216"),sQuery(id+"F6.wireOp",EDGE,"E217"),sQuery(id+"F6.wireOp",EDGE,"E218"),sQuery(id+"F6.wireOp",EDGE,"E219"),sQuery(id+"F6.wireOp",EDGE,"E220"),sQuery(id+"F6.wireOp",EDGE,"E221"),sQuery(id+"F6.wireOp",EDGE,"E222"),sQuery(id+"F6.wireOp",EDGE,"E223"),sQuery(id+"F6.wireOp",EDGE,"E224"),sQuery(id+"F6.wireOp",EDGE,"E225"),sQuery(id+"F6.wireOp",EDGE,"E226"),sQuery(id+"F6.wireOp",EDGE,"E227"),sQuery(id+"F6.wireOp",EDGE,"E228"),sQuery(id+"F6.wireOp",EDGE,"E239"),sQuery(id+"F6.wireOp",EDGE,"E240"),sQuery(id+"F6.wireOp",EDGE,"E241"),sQuery(id+"F6.wireOp",EDGE,"E242"),sQuery(id+"F6.wireOp",EDGE,"E243"),sQuery(id+"F6.wireOp",EDGE,"E244"),sQuery(id+"F6.wireOp",EDGE,"E245"),sQuery(id+"F6.wireOp",EDGE,"E246"),sQuery(id+"F6.wireOp",EDGE,"E247"),sQuery(id+"F6.wireOp",EDGE,"E248"),sQuery(id+"F6.wireOp",EDGE,"E249"),sQuery(id+"F6.wireOp",EDGE,"E250"),sQuery(id+"F6.wireOp",EDGE,"E251"),sQuery(id+"F6.wireOp",EDGE,"E252"),sQuery(id+"F6.wireOp",EDGE,"E253"),sQuery(id+"F6.wireOp",EDGE,"E254"),sQuery(id+"F6.wireOp",EDGE,"E255"),sQuery(id+"F6.wireOp",EDGE,"E256"),sQuery(id+"F6.wireOp",EDGE,"E257"),sQuery(id+"F6.wireOp",EDGE,"E258"),sQuery(id+"F6.wireOp",EDGE,"E259"),sQuery(id+"F6.wireOp",EDGE,"E260")])]});
            var Q1;
            Q1=makeQuery(id+"F9.opPattern","COPY",BODY,{"derivedFrom":makeQuery(id+"F7.opExtrude","SWEPT_BODY",BODY,{"disambiguationData":[OSD([sQuery(id+"F6.wireOp",EDGE,"E135"),sQuery(id+"F6.wireOp",EDGE,"E136"),sQuery(id+"F6.wireOp",EDGE,"E137"),sQuery(id+"F6.wireOp",EDGE,"E138"),sQuery(id+"F6.wireOp",EDGE,"E139"),sQuery(id+"F6.wireOp",EDGE,"E140"),sQuery(id+"F6.wireOp",EDGE,"E141"),sQuery(id+"F6.wireOp",EDGE,"E142"),sQuery(id+"F6.wireOp",EDGE,"E143"),sQuery(id+"F6.wireOp",EDGE,"E160"),sQuery(id+"F6.wireOp",EDGE,"E161"),sQuery(id+"F6.wireOp",EDGE,"E162"),sQuery(id+"F6.wireOp",EDGE,"E163"),sQuery(id+"F6.wireOp",EDGE,"E164"),sQuery(id+"F6.wireOp",EDGE,"E165"),sQuery(id+"F6.wireOp",EDGE,"E166"),sQuery(id+"F6.wireOp",EDGE,"E167"),sQuery(id+"F6.wireOp",EDGE,"E168"),sQuery(id+"F6.wireOp",EDGE,"E169"),sQuery(id+"F6.wireOp",EDGE,"E170"),sQuery(id+"F6.wireOp",EDGE,"E171"),sQuery(id+"F6.wireOp",EDGE,"E172"),sQuery(id+"F6.wireOp",EDGE,"E173"),sQuery(id+"F6.wireOp",EDGE,"E174"),sQuery(id+"F6.wireOp",EDGE,"E175"),sQuery(id+"F6.wireOp",EDGE,"E176"),sQuery(id+"F6.wireOp",EDGE,"E177"),sQuery(id+"F6.wireOp",EDGE,"E178"),sQuery(id+"F6.wireOp",EDGE,"E179"),sQuery(id+"F6.wireOp",EDGE,"E180"),sQuery(id+"F6.wireOp",EDGE,"E181"),sQuery(id+"F6.wireOp",EDGE,"E182"),sQuery(id+"F6.wireOp",EDGE,"E183"),sQuery(id+"F6.wireOp",EDGE,"E185"),sQuery(id+"F6.wireOp",EDGE,"E186"),sQuery(id+"F6.wireOp",EDGE,"E187"),sQuery(id+"F6.wireOp",EDGE,"E188"),sQuery(id+"F6.wireOp",EDGE,"E189"),sQuery(id+"F6.wireOp",EDGE,"E190"),sQuery(id+"F6.wireOp",EDGE,"E191"),sQuery(id+"F6.wireOp",EDGE,"E192"),sQuery(id+"F6.wireOp",EDGE,"E193"),sQuery(id+"F6.wireOp",EDGE,"E194"),sQuery(id+"F6.wireOp",EDGE,"E195"),sQuery(id+"F6.wireOp",EDGE,"E196"),sQuery(id+"F6.wireOp",EDGE,"E197"),sQuery(id+"F6.wireOp",EDGE,"E198"),sQuery(id+"F6.wireOp",EDGE,"E199"),sQuery(id+"F6.wireOp",EDGE,"E200"),sQuery(id+"F6.wireOp",EDGE,"E201"),sQuery(id+"F6.wireOp",EDGE,"E202"),sQuery(id+"F6.wireOp",EDGE,"E203"),sQuery(id+"F6.wireOp",EDGE,"E204"),sQuery(id+"F6.wireOp",EDGE,"E216"),sQuery(id+"F6.wireOp",EDGE,"E217"),sQuery(id+"F6.wireOp",EDGE,"E218"),sQuery(id+"F6.wireOp",EDGE,"E219"),sQuery(id+"F6.wireOp",EDGE,"E220"),sQuery(id+"F6.wireOp",EDGE,"E221"),sQuery(id+"F6.wireOp",EDGE,"E222"),sQuery(id+"F6.wireOp",EDGE,"E223"),sQuery(id+"F6.wireOp",EDGE,"E224"),sQuery(id+"F6.wireOp",EDGE,"E225"),sQuery(id+"F6.wireOp",EDGE,"E226"),sQuery(id+"F6.wireOp",EDGE,"E227"),sQuery(id+"F6.wireOp",EDGE,"E228"),sQuery(id+"F6.wireOp",EDGE,"E239"),sQuery(id+"F6.wireOp",EDGE,"E240"),sQuery(id+"F6.wireOp",EDGE,"E241"),sQuery(id+"F6.wireOp",EDGE,"E242"),sQuery(id+"F6.wireOp",EDGE,"E243"),sQuery(id+"F6.wireOp",EDGE,"E244"),sQuery(id+"F6.wireOp",EDGE,"E245"),sQuery(id+"F6.wireOp",EDGE,"E246"),sQuery(id+"F6.wireOp",EDGE,"E247"),sQuery(id+"F6.wireOp",EDGE,"E248"),sQuery(id+"F6.wireOp",EDGE,"E249"),sQuery(id+"F6.wireOp",EDGE,"E250"),sQuery(id+"F6.wireOp",EDGE,"E251"),sQuery(id+"F6.wireOp",EDGE,"E252"),sQuery(id+"F6.wireOp",EDGE,"E253"),sQuery(id+"F6.wireOp",EDGE,"E254"),sQuery(id+"F6.wireOp",EDGE,"E255"),sQuery(id+"F6.wireOp",EDGE,"E256"),sQuery(id+"F6.wireOp",EDGE,"E257"),sQuery(id+"F6.wireOp",EDGE,"E258"),sQuery(id+"F6.wireOp",EDGE,"E259"),sQuery(id+"F6.wireOp",EDGE,"E260")])]}),"instanceName":"1"});
            transform(context, id + "F11", {"entities" : qUnion([Q0, Q1]), "transformType" : TransformType.TRANSLATION_3D, "dx" : -353 * mm, "dy" : 0 * mm, "dz" : 0 * mm, "makeCopy" : true});
        }
        {
            var Q0;
            Q0=qCreatedBy(makeId("Top.planeOp"),FACE);
            cPlane(context, id + "F12", {"entities" : qUnion([Q0]), "cplaneType" : CPlaneType.OFFSET, "offset" : 18.6 * mm, "oppositeDirection" : true, "width" : 150 * mm, "height" : 150 * mm});
        }
        {
            var Q0;
            Q0=qCreatedBy(id+"F12.planeOp",FACE);
            var sketch = newSketch(context, id + "F13", { "sketchPlane" : qUnion([Q0])});
            skLineSegment(sketch, "E262", {"start": v(25.7, -17.22) * mm, "end": v(25.7, -25.12) * mm});
            skLineSegment(sketch, "E263", {"start": v(22.1, -21.63) * mm, "end": v(30.9, -21.63) * mm});
            skLineSegment(sketch, "E264", {"start": v(25.7, -40.02) * mm, "end": v(25.7, -32.12) * mm});
            skLineSegment(sketch, "E265", {"start": v(22.1, -35.63) * mm, "end": v(30.9, -35.63) * mm});
            skLineSegment(sketch, "E266", {"start": v(28.7, -30.77) * mm, "end": v(27.2, -30.77) * mm});
            skLineSegment(sketch, "E267", {"start": v(27.2, -32.77) * mm, "end": v(23.2, -32.77) * mm});
            skLineSegment(sketch, "E268", {"start": v(27.2, -32.77) * mm, "end": v(27.2, -30.77) * mm});
            skLineSegment(sketch, "E269", {"start": v(28.7, -26.48) * mm, "end": v(27.2, -26.48) * mm});
            skLineSegment(sketch, "E270", {"start": v(27.2, -24.48) * mm, "end": v(23.2, -24.48) * mm});
            skLineSegment(sketch, "E271", {"start": v(27.2, -24.48) * mm, "end": v(27.2, -26.48) * mm});
            skLineSegment(sketch, "E272", {"start": v(23.2, -24.48) * mm, "end": v(23.2, -26.12) * mm});
            skLineSegment(sketch, "E273", {"start": v(23.2, -26.12) * mm, "end": v(21.9, -26.12) * mm});
            skLineSegment(sketch, "E274", {"start": v(23.2, -32.77) * mm, "end": v(21.9, -26.12) * mm});
            skLineSegment(sketch, "E275", {"start": v(27.34, -20.94) * mm, "end": v(26.38, -19.97) * mm});
            skLineSegment(sketch, "E276", {"start": v(26.38, -19.97) * mm, "end": v(25, -19.97) * mm});
            skLineSegment(sketch, "E277", {"start": v(25, -19.97) * mm, "end": v(24.04, -20.94) * mm});
            skLineSegment(sketch, "E278", {"start": v(24.04, -20.94) * mm, "end": v(24.04, -22.3) * mm});
            skLineSegment(sketch, "E279", {"start": v(24.04, -22.3) * mm, "end": v(25, -23.28) * mm});
            skLineSegment(sketch, "E280", {"start": v(25, -23.28) * mm, "end": v(26.38, -23.28) * mm});
            skLineSegment(sketch, "E281", {"start": v(26.38, -23.28) * mm, "end": v(27.34, -22.3) * mm});
            skLineSegment(sketch, "E282", {"start": v(27.34, -22.3) * mm, "end": v(27.34, -20.94) * mm});
            skLineSegment(sketch, "E283", {"start": v(27.34, -34.94) * mm, "end": v(26.38, -33.98) * mm});
            skLineSegment(sketch, "E284", {"start": v(26.38, -33.98) * mm, "end": v(25, -33.98) * mm});
            skLineSegment(sketch, "E285", {"start": v(25, -33.98) * mm, "end": v(24.04, -34.94) * mm});
            skLineSegment(sketch, "E286", {"start": v(24.04, -34.94) * mm, "end": v(24.04, -36.3) * mm});
            skLineSegment(sketch, "E287", {"start": v(24.04, -36.3) * mm, "end": v(25, -37.28) * mm});
            skLineSegment(sketch, "E288", {"start": v(25, -37.28) * mm, "end": v(26.38, -37.28) * mm});
            skLineSegment(sketch, "E289", {"start": v(26.38, -37.28) * mm, "end": v(27.34, -36.3) * mm});
            skLineSegment(sketch, "E290", {"start": v(27.34, -36.3) * mm, "end": v(27.34, -34.94) * mm});
            skLineSegment(sketch, "E291", {"start": v(27.7, -18.62) * mm, "end": v(28.7, -19.62) * mm});
            skLineSegment(sketch, "E292", {"start": v(28.7, -37.62) * mm, "end": v(27.7, -38.62) * mm});
            skLineSegment(sketch, "E293", {"start": v(25.7, -18.83) * mm, "end": v(26.44, -18.83) * mm});
            skLineSegment(sketch, "E294", {"start": v(26.44, -18.83) * mm, "end": v(26.44, -18.62) * mm});
            skLineSegment(sketch, "E295", {"start": v(25.7, -18.83) * mm, "end": v(24.94, -18.83) * mm});
            skLineSegment(sketch, "E296", {"start": v(24.94, -18.83) * mm, "end": v(24.94, -18.62) * mm});
            skLineSegment(sketch, "E297", {"start": v(27.7, -18.62) * mm, "end": v(26.44, -18.62) * mm});
            skLineSegment(sketch, "E298", {"start": v(28.5, -21.63) * mm, "end": v(28.5, -22.38) * mm});
            skLineSegment(sketch, "E299", {"start": v(28.5, -22.38) * mm, "end": v(28.7, -22.38) * mm});
            skLineSegment(sketch, "E300", {"start": v(28.5, -21.63) * mm, "end": v(28.5, -20.88) * mm});
            skLineSegment(sketch, "E301", {"start": v(28.5, -20.88) * mm, "end": v(28.7, -20.88) * mm});
            skLineSegment(sketch, "E302", {"start": v(28.5, -35.63) * mm, "end": v(28.5, -34.88) * mm});
            skLineSegment(sketch, "E303", {"start": v(28.5, -34.88) * mm, "end": v(28.7, -34.88) * mm});
            skLineSegment(sketch, "E304", {"start": v(28.5, -35.63) * mm, "end": v(28.5, -36.38) * mm});
            skLineSegment(sketch, "E305", {"start": v(28.5, -36.38) * mm, "end": v(28.7, -36.38) * mm});
            skLineSegment(sketch, "E306", {"start": v(25.7, -38.43) * mm, "end": v(26.44, -38.43) * mm});
            skLineSegment(sketch, "E307", {"start": v(26.44, -38.43) * mm, "end": v(26.44, -38.62) * mm});
            skLineSegment(sketch, "E308", {"start": v(25.7, -38.43) * mm, "end": v(24.94, -38.43) * mm});
            skLineSegment(sketch, "E309", {"start": v(24.94, -38.43) * mm, "end": v(24.94, -38.62) * mm});
            skLineSegment(sketch, "E310", {"start": v(28.7, -19.62) * mm, "end": v(28.7, -20.88) * mm});
            skLineSegment(sketch, "E311", {"start": v(28.7, -22.38) * mm, "end": v(28.7, -26.48) * mm});
            skLineSegment(sketch, "E312", {"start": v(27.7, -38.62) * mm, "end": v(26.44, -38.62) * mm});
            skLineSegment(sketch, "E313", {"start": v(28.7, -37.62) * mm, "end": v(28.7, -36.38) * mm});
            skLineSegment(sketch, "E314", {"start": v(28.7, -34.88) * mm, "end": v(28.7, -30.77) * mm});
            skLineSegment(sketch, "E315", {"start": v(18.7, -13.92) * mm, "end": v(18.7, -42.92) * mm});
            skLineSegment(sketch, "E316", {"start": v(20.84, -18.62) * mm, "end": v(20.84, -20.12) * mm});
            skLineSegment(sketch, "E317", {"start": v(22.84, -20.12) * mm, "end": v(22.84, -24.12) * mm});
            skLineSegment(sketch, "E318", {"start": v(22.84, -20.12) * mm, "end": v(20.84, -20.12) * mm});
            skLineSegment(sketch, "E319", {"start": v(16.54, -18.62) * mm, "end": v(16.54, -20.12) * mm});
            skLineSegment(sketch, "E320", {"start": v(14.54, -20.12) * mm, "end": v(14.54, -24.12) * mm});
            skLineSegment(sketch, "E321", {"start": v(14.54, -20.12) * mm, "end": v(16.54, -20.12) * mm});
            skLineSegment(sketch, "E322", {"start": v(14.54, -24.12) * mm, "end": v(16.2, -24.12) * mm});
            skLineSegment(sketch, "E323", {"start": v(16.2, -24.12) * mm, "end": v(16.2, -25.42) * mm});
            skLineSegment(sketch, "E324", {"start": v(22.84, -24.12) * mm, "end": v(16.2, -25.42) * mm});
            skLineSegment(sketch, "E325", {"start": v(16.54, -38.62) * mm, "end": v(16.54, -37.12) * mm});
            skLineSegment(sketch, "E326", {"start": v(14.54, -37.12) * mm, "end": v(14.54, -33.12) * mm});
            skLineSegment(sketch, "E327", {"start": v(14.54, -37.12) * mm, "end": v(16.54, -37.12) * mm});
            skLineSegment(sketch, "E328", {"start": v(20.84, -38.62) * mm, "end": v(20.84, -37.12) * mm});
            skLineSegment(sketch, "E329", {"start": v(22.84, -37.12) * mm, "end": v(22.84, -33.12) * mm});
            skLineSegment(sketch, "E330", {"start": v(22.84, -37.12) * mm, "end": v(20.84, -37.12) * mm});
            skLineSegment(sketch, "E331", {"start": v(22.84, -33.12) * mm, "end": v(21.2, -33.12) * mm});
            skLineSegment(sketch, "E332", {"start": v(21.2, -33.12) * mm, "end": v(21.2, -31.83) * mm});
            skLineSegment(sketch, "E333", {"start": v(14.54, -33.12) * mm, "end": v(21.2, -31.83) * mm});
            skLineSegment(sketch, "E334", {"start": v(24.94, -18.62) * mm, "end": v(20.84, -18.62) * mm});
            skLineSegment(sketch, "E335", {"start": v(24.94, -38.62) * mm, "end": v(20.84, -38.62) * mm});
            skLineSegment(sketch, "E336", {"start": v(6.1, -28.62) * mm, "end": v(31.6, -28.62) * mm});
            skLineSegment(sketch, "E337", {"start": v(11.7, -17.22) * mm, "end": v(11.7, -25.12) * mm});
            skLineSegment(sketch, "E338", {"start": v(15.3, -21.63) * mm, "end": v(6.5, -21.63) * mm});
            skLineSegment(sketch, "E339", {"start": v(10.04, -20.94) * mm, "end": v(11, -19.97) * mm});
            skLineSegment(sketch, "E340", {"start": v(11, -19.97) * mm, "end": v(12.38, -19.97) * mm});
            skLineSegment(sketch, "E341", {"start": v(12.38, -19.97) * mm, "end": v(13.34, -20.94) * mm});
            skLineSegment(sketch, "E342", {"start": v(13.34, -20.94) * mm, "end": v(13.34, -22.3) * mm});
            skLineSegment(sketch, "E343", {"start": v(13.34, -22.3) * mm, "end": v(12.38, -23.28) * mm});
            skLineSegment(sketch, "E344", {"start": v(12.38, -23.28) * mm, "end": v(11, -23.28) * mm});
            skLineSegment(sketch, "E345", {"start": v(11, -23.28) * mm, "end": v(10.04, -22.3) * mm});
            skLineSegment(sketch, "E346", {"start": v(10.04, -22.3) * mm, "end": v(10.04, -20.94) * mm});
            skLineSegment(sketch, "E347", {"start": v(9.7, -18.62) * mm, "end": v(8.7, -19.62) * mm});
            skLineSegment(sketch, "E348", {"start": v(11.7, -18.83) * mm, "end": v(10.94, -18.83) * mm});
            skLineSegment(sketch, "E349", {"start": v(10.94, -18.83) * mm, "end": v(10.94, -18.62) * mm});
            skLineSegment(sketch, "E350", {"start": v(11.7, -18.83) * mm, "end": v(12.44, -18.83) * mm});
            skLineSegment(sketch, "E351", {"start": v(12.44, -18.83) * mm, "end": v(12.44, -18.62) * mm});
            skLineSegment(sketch, "E352", {"start": v(9.7, -18.62) * mm, "end": v(10.94, -18.62) * mm});
            skLineSegment(sketch, "E353", {"start": v(8.9, -21.63) * mm, "end": v(8.9, -22.38) * mm});
            skLineSegment(sketch, "E354", {"start": v(8.9, -22.38) * mm, "end": v(8.7, -22.38) * mm});
            skLineSegment(sketch, "E355", {"start": v(8.9, -21.63) * mm, "end": v(8.9, -20.88) * mm});
            skLineSegment(sketch, "E356", {"start": v(8.9, -20.88) * mm, "end": v(8.7, -20.88) * mm});
            skLineSegment(sketch, "E357", {"start": v(8.7, -19.62) * mm, "end": v(8.7, -20.88) * mm});
            skLineSegment(sketch, "E358", {"start": v(8.7, -22.38) * mm, "end": v(8.7, -26.48) * mm});
            skLineSegment(sketch, "E359", {"start": v(12.44, -18.62) * mm, "end": v(16.54, -18.62) * mm});
            skLineSegment(sketch, "E360", {"start": v(11.7, -40.02) * mm, "end": v(11.7, -32.12) * mm});
            skLineSegment(sketch, "E361", {"start": v(15.3, -35.63) * mm, "end": v(6.5, -35.63) * mm});
            skLineSegment(sketch, "E362", {"start": v(10.04, -34.94) * mm, "end": v(11, -33.98) * mm});
            skLineSegment(sketch, "E363", {"start": v(11, -33.98) * mm, "end": v(12.38, -33.98) * mm});
            skLineSegment(sketch, "E364", {"start": v(12.38, -33.98) * mm, "end": v(13.34, -34.94) * mm});
            skLineSegment(sketch, "E365", {"start": v(13.34, -34.94) * mm, "end": v(13.34, -36.3) * mm});
            skLineSegment(sketch, "E366", {"start": v(13.34, -36.3) * mm, "end": v(12.38, -37.28) * mm});
            skLineSegment(sketch, "E367", {"start": v(12.38, -37.28) * mm, "end": v(11, -37.28) * mm});
            skLineSegment(sketch, "E368", {"start": v(11, -37.28) * mm, "end": v(10.04, -36.3) * mm});
            skLineSegment(sketch, "E369", {"start": v(10.04, -36.3) * mm, "end": v(10.04, -34.94) * mm});
            skLineSegment(sketch, "E370", {"start": v(8.7, -37.62) * mm, "end": v(9.7, -38.62) * mm});
            skLineSegment(sketch, "E371", {"start": v(8.9, -35.63) * mm, "end": v(8.9, -34.88) * mm});
            skLineSegment(sketch, "E372", {"start": v(8.9, -34.88) * mm, "end": v(8.7, -34.88) * mm});
            skLineSegment(sketch, "E373", {"start": v(8.9, -35.63) * mm, "end": v(8.9, -36.38) * mm});
            skLineSegment(sketch, "E374", {"start": v(8.9, -36.38) * mm, "end": v(8.7, -36.38) * mm});
            skLineSegment(sketch, "E375", {"start": v(11.7, -38.43) * mm, "end": v(10.94, -38.43) * mm});
            skLineSegment(sketch, "E376", {"start": v(10.94, -38.43) * mm, "end": v(10.94, -38.62) * mm});
            skLineSegment(sketch, "E377", {"start": v(11.7, -38.43) * mm, "end": v(12.44, -38.43) * mm});
            skLineSegment(sketch, "E378", {"start": v(12.44, -38.43) * mm, "end": v(12.44, -38.62) * mm});
            skLineSegment(sketch, "E379", {"start": v(9.7, -38.62) * mm, "end": v(10.94, -38.62) * mm});
            skLineSegment(sketch, "E380", {"start": v(8.7, -37.62) * mm, "end": v(8.7, -36.38) * mm});
            skLineSegment(sketch, "E381", {"start": v(8.7, -34.88) * mm, "end": v(8.7, -30.77) * mm});
            skLineSegment(sketch, "E382", {"start": v(12.44, -38.62) * mm, "end": v(16.54, -38.62) * mm});
            skLineSegment(sketch, "E383", {"start": v(8.7, -26.48) * mm, "end": v(10.2, -26.48) * mm});
            skLineSegment(sketch, "E384", {"start": v(10.2, -24.48) * mm, "end": v(14.2, -24.48) * mm});
            skLineSegment(sketch, "E385", {"start": v(10.2, -24.48) * mm, "end": v(10.2, -26.48) * mm});
            skLineSegment(sketch, "E386", {"start": v(8.7, -30.77) * mm, "end": v(10.2, -30.77) * mm});
            skLineSegment(sketch, "E387", {"start": v(10.2, -32.77) * mm, "end": v(14.2, -32.77) * mm});
            skLineSegment(sketch, "E388", {"start": v(10.2, -32.77) * mm, "end": v(10.2, -30.77) * mm});
            skLineSegment(sketch, "E389", {"start": v(14.2, -32.77) * mm, "end": v(14.2, -31.12) * mm});
            skLineSegment(sketch, "E390", {"start": v(14.2, -31.12) * mm, "end": v(15.5, -31.12) * mm});
            skLineSegment(sketch, "E391", {"start": v(14.2, -24.48) * mm, "end": v(15.5, -31.12) * mm});
            skCircle(sketch, "E392", {"center": v(18.7, -28.62) * mm, "radius": 1.6 * mm});
            skSolve(sketch);
        }
        {
            var Q0;
            Q0 = qSketchRegion(id + "F13", true);
            extrude(context, id + "F14", {"entities" : qUnion([Q0]), "depth" : 460 * mm, "offsetDistance" : 25 * mm});
        }
        {
            var Q0;
            Q0=makeQuery(id+"F14.opExtrude","SWEPT_BODY",BODY,{"disambiguationData":[OSD([sQuery(id+"F13.wireOp",EDGE,"E266"),sQuery(id+"F13.wireOp",EDGE,"E267"),sQuery(id+"F13.wireOp",EDGE,"E268"),sQuery(id+"F13.wireOp",EDGE,"E269"),sQuery(id+"F13.wireOp",EDGE,"E270"),sQuery(id+"F13.wireOp",EDGE,"E271"),sQuery(id+"F13.wireOp",EDGE,"E272"),sQuery(id+"F13.wireOp",EDGE,"E273"),sQuery(id+"F13.wireOp",EDGE,"E274"),sQuery(id+"F13.wireOp",EDGE,"E275"),sQuery(id+"F13.wireOp",EDGE,"E276"),sQuery(id+"F13.wireOp",EDGE,"E277"),sQuery(id+"F13.wireOp",EDGE,"E278"),sQuery(id+"F13.wireOp",EDGE,"E279"),sQuery(id+"F13.wireOp",EDGE,"E280"),sQuery(id+"F13.wireOp",EDGE,"E281"),sQuery(id+"F13.wireOp",EDGE,"E282"),sQuery(id+"F13.wireOp",EDGE,"E283"),sQuery(id+"F13.wireOp",EDGE,"E284"),sQuery(id+"F13.wireOp",EDGE,"E285"),sQuery(id+"F13.wireOp",EDGE,"E286"),sQuery(id+"F13.wireOp",EDGE,"E287"),sQuery(id+"F13.wireOp",EDGE,"E288"),sQuery(id+"F13.wireOp",EDGE,"E289"),sQuery(id+"F13.wireOp",EDGE,"E290"),sQuery(id+"F13.wireOp",EDGE,"E291"),sQuery(id+"F13.wireOp",EDGE,"E292"),sQuery(id+"F13.wireOp",EDGE,"E293"),sQuery(id+"F13.wireOp",EDGE,"E294"),sQuery(id+"F13.wireOp",EDGE,"E295"),sQuery(id+"F13.wireOp",EDGE,"E296"),sQuery(id+"F13.wireOp",EDGE,"E297"),sQuery(id+"F13.wireOp",EDGE,"E298"),sQuery(id+"F13.wireOp",EDGE,"E299"),sQuery(id+"F13.wireOp",EDGE,"E300"),sQuery(id+"F13.wireOp",EDGE,"E301"),sQuery(id+"F13.wireOp",EDGE,"E302"),sQuery(id+"F13.wireOp",EDGE,"E303"),sQuery(id+"F13.wireOp",EDGE,"E304"),sQuery(id+"F13.wireOp",EDGE,"E305"),sQuery(id+"F13.wireOp",EDGE,"E306"),sQuery(id+"F13.wireOp",EDGE,"E307"),sQuery(id+"F13.wireOp",EDGE,"E308"),sQuery(id+"F13.wireOp",EDGE,"E309"),sQuery(id+"F13.wireOp",EDGE,"E310"),sQuery(id+"F13.wireOp",EDGE,"E311"),sQuery(id+"F13.wireOp",EDGE,"E312"),sQuery(id+"F13.wireOp",EDGE,"E313"),sQuery(id+"F13.wireOp",EDGE,"E314"),sQuery(id+"F13.wireOp",EDGE,"E316"),sQuery(id+"F13.wireOp",EDGE,"E317"),sQuery(id+"F13.wireOp",EDGE,"E318"),sQuery(id+"F13.wireOp",EDGE,"E319"),sQuery(id+"F13.wireOp",EDGE,"E320"),sQuery(id+"F13.wireOp",EDGE,"E321"),sQuery(id+"F13.wireOp",EDGE,"E322"),sQuery(id+"F13.wireOp",EDGE,"E323"),sQuery(id+"F13.wireOp",EDGE,"E324"),sQuery(id+"F13.wireOp",EDGE,"E325"),sQuery(id+"F13.wireOp",EDGE,"E326"),sQuery(id+"F13.wireOp",EDGE,"E327"),sQuery(id+"F13.wireOp",EDGE,"E328"),sQuery(id+"F13.wireOp",EDGE,"E329"),sQuery(id+"F13.wireOp",EDGE,"E330"),sQuery(id+"F13.wireOp",EDGE,"E331"),sQuery(id+"F13.wireOp",EDGE,"E332"),sQuery(id+"F13.wireOp",EDGE,"E333"),sQuery(id+"F13.wireOp",EDGE,"E334"),sQuery(id+"F13.wireOp",EDGE,"E335"),sQuery(id+"F13.wireOp",EDGE,"E339"),sQuery(id+"F13.wireOp",EDGE,"E340"),sQuery(id+"F13.wireOp",EDGE,"E341"),sQuery(id+"F13.wireOp",EDGE,"E342"),sQuery(id+"F13.wireOp",EDGE,"E343"),sQuery(id+"F13.wireOp",EDGE,"E344"),sQuery(id+"F13.wireOp",EDGE,"E345"),sQuery(id+"F13.wireOp",EDGE,"E346"),sQuery(id+"F13.wireOp",EDGE,"E347"),sQuery(id+"F13.wireOp",EDGE,"E348"),sQuery(id+"F13.wireOp",EDGE,"E349"),sQuery(id+"F13.wireOp",EDGE,"E350"),sQuery(id+"F13.wireOp",EDGE,"E351"),sQuery(id+"F13.wireOp",EDGE,"E352"),sQuery(id+"F13.wireOp",EDGE,"E353"),sQuery(id+"F13.wireOp",EDGE,"E354"),sQuery(id+"F13.wireOp",EDGE,"E355"),sQuery(id+"F13.wireOp",EDGE,"E356"),sQuery(id+"F13.wireOp",EDGE,"E357"),sQuery(id+"F13.wireOp",EDGE,"E358"),sQuery(id+"F13.wireOp",EDGE,"E359"),sQuery(id+"F13.wireOp",EDGE,"E362"),sQuery(id+"F13.wireOp",EDGE,"E363"),sQuery(id+"F13.wireOp",EDGE,"E364"),sQuery(id+"F13.wireOp",EDGE,"E365"),sQuery(id+"F13.wireOp",EDGE,"E366"),sQuery(id+"F13.wireOp",EDGE,"E367"),sQuery(id+"F13.wireOp",EDGE,"E368"),sQuery(id+"F13.wireOp",EDGE,"E369"),sQuery(id+"F13.wireOp",EDGE,"E370"),sQuery(id+"F13.wireOp",EDGE,"E371"),sQuery(id+"F13.wireOp",EDGE,"E372"),sQuery(id+"F13.wireOp",EDGE,"E373"),sQuery(id+"F13.wireOp",EDGE,"E374"),sQuery(id+"F13.wireOp",EDGE,"E375"),sQuery(id+"F13.wireOp",EDGE,"E376"),sQuery(id+"F13.wireOp",EDGE,"E377"),sQuery(id+"F13.wireOp",EDGE,"E378"),sQuery(id+"F13.wireOp",EDGE,"E379"),sQuery(id+"F13.wireOp",EDGE,"E380"),sQuery(id+"F13.wireOp",EDGE,"E381"),sQuery(id+"F13.wireOp",EDGE,"E382"),sQuery(id+"F13.wireOp",EDGE,"E383"),sQuery(id+"F13.wireOp",EDGE,"E384"),sQuery(id+"F13.wireOp",EDGE,"E385"),sQuery(id+"F13.wireOp",EDGE,"E386"),sQuery(id+"F13.wireOp",EDGE,"E387"),sQuery(id+"F13.wireOp",EDGE,"E388"),sQuery(id+"F13.wireOp",EDGE,"E389"),sQuery(id+"F13.wireOp",EDGE,"E390"),sQuery(id+"F13.wireOp",EDGE,"E391"),sQuery(id+"F13.wireOp",EDGE,"E392")])]});
            transform(context, id + "F15", {"entities" : qUnion([Q0]), "transformType" : TransformType.TRANSLATION_3D, "dx" : -28.7 * mm, "dy" : 47.3 * mm, "dz" : 0 * mm, "makeCopy" : false});
        }
        {
            var Q0;
            Q0=makeQuery(id+"F14.opExtrude","SWEPT_BODY",BODY,{"disambiguationData":[OSD([sQuery(id+"F13.wireOp",EDGE,"E266"),sQuery(id+"F13.wireOp",EDGE,"E267"),sQuery(id+"F13.wireOp",EDGE,"E268"),sQuery(id+"F13.wireOp",EDGE,"E269"),sQuery(id+"F13.wireOp",EDGE,"E270"),sQuery(id+"F13.wireOp",EDGE,"E271"),sQuery(id+"F13.wireOp",EDGE,"E272"),sQuery(id+"F13.wireOp",EDGE,"E273"),sQuery(id+"F13.wireOp",EDGE,"E274"),sQuery(id+"F13.wireOp",EDGE,"E275"),sQuery(id+"F13.wireOp",EDGE,"E276"),sQuery(id+"F13.wireOp",EDGE,"E277"),sQuery(id+"F13.wireOp",EDGE,"E278"),sQuery(id+"F13.wireOp",EDGE,"E279"),sQuery(id+"F13.wireOp",EDGE,"E280"),sQuery(id+"F13.wireOp",EDGE,"E281"),sQuery(id+"F13.wireOp",EDGE,"E282"),sQuery(id+"F13.wireOp",EDGE,"E283"),sQuery(id+"F13.wireOp",EDGE,"E284"),sQuery(id+"F13.wireOp",EDGE,"E285"),sQuery(id+"F13.wireOp",EDGE,"E286"),sQuery(id+"F13.wireOp",EDGE,"E287"),sQuery(id+"F13.wireOp",EDGE,"E288"),sQuery(id+"F13.wireOp",EDGE,"E289"),sQuery(id+"F13.wireOp",EDGE,"E290"),sQuery(id+"F13.wireOp",EDGE,"E291"),sQuery(id+"F13.wireOp",EDGE,"E292"),sQuery(id+"F13.wireOp",EDGE,"E293"),sQuery(id+"F13.wireOp",EDGE,"E294"),sQuery(id+"F13.wireOp",EDGE,"E295"),sQuery(id+"F13.wireOp",EDGE,"E296"),sQuery(id+"F13.wireOp",EDGE,"E297"),sQuery(id+"F13.wireOp",EDGE,"E298"),sQuery(id+"F13.wireOp",EDGE,"E299"),sQuery(id+"F13.wireOp",EDGE,"E300"),sQuery(id+"F13.wireOp",EDGE,"E301"),sQuery(id+"F13.wireOp",EDGE,"E302"),sQuery(id+"F13.wireOp",EDGE,"E303"),sQuery(id+"F13.wireOp",EDGE,"E304"),sQuery(id+"F13.wireOp",EDGE,"E305"),sQuery(id+"F13.wireOp",EDGE,"E306"),sQuery(id+"F13.wireOp",EDGE,"E307"),sQuery(id+"F13.wireOp",EDGE,"E308"),sQuery(id+"F13.wireOp",EDGE,"E309"),sQuery(id+"F13.wireOp",EDGE,"E310"),sQuery(id+"F13.wireOp",EDGE,"E311"),sQuery(id+"F13.wireOp",EDGE,"E312"),sQuery(id+"F13.wireOp",EDGE,"E313"),sQuery(id+"F13.wireOp",EDGE,"E314"),sQuery(id+"F13.wireOp",EDGE,"E316"),sQuery(id+"F13.wireOp",EDGE,"E317"),sQuery(id+"F13.wireOp",EDGE,"E318"),sQuery(id+"F13.wireOp",EDGE,"E319"),sQuery(id+"F13.wireOp",EDGE,"E320"),sQuery(id+"F13.wireOp",EDGE,"E321"),sQuery(id+"F13.wireOp",EDGE,"E322"),sQuery(id+"F13.wireOp",EDGE,"E323"),sQuery(id+"F13.wireOp",EDGE,"E324"),sQuery(id+"F13.wireOp",EDGE,"E325"),sQuery(id+"F13.wireOp",EDGE,"E326"),sQuery(id+"F13.wireOp",EDGE,"E327"),sQuery(id+"F13.wireOp",EDGE,"E328"),sQuery(id+"F13.wireOp",EDGE,"E329"),sQuery(id+"F13.wireOp",EDGE,"E330"),sQuery(id+"F13.wireOp",EDGE,"E331"),sQuery(id+"F13.wireOp",EDGE,"E332"),sQuery(id+"F13.wireOp",EDGE,"E333"),sQuery(id+"F13.wireOp",EDGE,"E334"),sQuery(id+"F13.wireOp",EDGE,"E335"),sQuery(id+"F13.wireOp",EDGE,"E339"),sQuery(id+"F13.wireOp",EDGE,"E340"),sQuery(id+"F13.wireOp",EDGE,"E341"),sQuery(id+"F13.wireOp",EDGE,"E342"),sQuery(id+"F13.wireOp",EDGE,"E343"),sQuery(id+"F13.wireOp",EDGE,"E344"),sQuery(id+"F13.wireOp",EDGE,"E345"),sQuery(id+"F13.wireOp",EDGE,"E346"),sQuery(id+"F13.wireOp",EDGE,"E347"),sQuery(id+"F13.wireOp",EDGE,"E348"),sQuery(id+"F13.wireOp",EDGE,"E349"),sQuery(id+"F13.wireOp",EDGE,"E350"),sQuery(id+"F13.wireOp",EDGE,"E351"),sQuery(id+"F13.wireOp",EDGE,"E352"),sQuery(id+"F13.wireOp",EDGE,"E353"),sQuery(id+"F13.wireOp",EDGE,"E354"),sQuery(id+"F13.wireOp",EDGE,"E355"),sQuery(id+"F13.wireOp",EDGE,"E356"),sQuery(id+"F13.wireOp",EDGE,"E357"),sQuery(id+"F13.wireOp",EDGE,"E358"),sQuery(id+"F13.wireOp",EDGE,"E359"),sQuery(id+"F13.wireOp",EDGE,"E362"),sQuery(id+"F13.wireOp",EDGE,"E363"),sQuery(id+"F13.wireOp",EDGE,"E364"),sQuery(id+"F13.wireOp",EDGE,"E365"),sQuery(id+"F13.wireOp",EDGE,"E366"),sQuery(id+"F13.wireOp",EDGE,"E367"),sQuery(id+"F13.wireOp",EDGE,"E368"),sQuery(id+"F13.wireOp",EDGE,"E369"),sQuery(id+"F13.wireOp",EDGE,"E370"),sQuery(id+"F13.wireOp",EDGE,"E371"),sQuery(id+"F13.wireOp",EDGE,"E372"),sQuery(id+"F13.wireOp",EDGE,"E373"),sQuery(id+"F13.wireOp",EDGE,"E374"),sQuery(id+"F13.wireOp",EDGE,"E375"),sQuery(id+"F13.wireOp",EDGE,"E376"),sQuery(id+"F13.wireOp",EDGE,"E377"),sQuery(id+"F13.wireOp",EDGE,"E378"),sQuery(id+"F13.wireOp",EDGE,"E379"),sQuery(id+"F13.wireOp",EDGE,"E380"),sQuery(id+"F13.wireOp",EDGE,"E381"),sQuery(id+"F13.wireOp",EDGE,"E382"),sQuery(id+"F13.wireOp",EDGE,"E383"),sQuery(id+"F13.wireOp",EDGE,"E384"),sQuery(id+"F13.wireOp",EDGE,"E385"),sQuery(id+"F13.wireOp",EDGE,"E386"),sQuery(id+"F13.wireOp",EDGE,"E387"),sQuery(id+"F13.wireOp",EDGE,"E388"),sQuery(id+"F13.wireOp",EDGE,"E389"),sQuery(id+"F13.wireOp",EDGE,"E390"),sQuery(id+"F13.wireOp",EDGE,"E391"),sQuery(id+"F13.wireOp",EDGE,"E392")])]});
            transform(context, id + "F16", {"entities" : qUnion([Q0]), "transformType" : TransformType.TRANSLATION_3D, "dx" : 0 * mm, "dy" : 650 * mm, "dz" : 0 * mm, "makeCopy" : true});
        }
        {
            var Q0;
            Q0=makeQuery(id+"F14.opExtrude","SWEPT_BODY",BODY,{"disambiguationData":[OSD([sQuery(id+"F13.wireOp",EDGE,"E266"),sQuery(id+"F13.wireOp",EDGE,"E267"),sQuery(id+"F13.wireOp",EDGE,"E268"),sQuery(id+"F13.wireOp",EDGE,"E269"),sQuery(id+"F13.wireOp",EDGE,"E270"),sQuery(id+"F13.wireOp",EDGE,"E271"),sQuery(id+"F13.wireOp",EDGE,"E272"),sQuery(id+"F13.wireOp",EDGE,"E273"),sQuery(id+"F13.wireOp",EDGE,"E274"),sQuery(id+"F13.wireOp",EDGE,"E275"),sQuery(id+"F13.wireOp",EDGE,"E276"),sQuery(id+"F13.wireOp",EDGE,"E277"),sQuery(id+"F13.wireOp",EDGE,"E278"),sQuery(id+"F13.wireOp",EDGE,"E279"),sQuery(id+"F13.wireOp",EDGE,"E280"),sQuery(id+"F13.wireOp",EDGE,"E281"),sQuery(id+"F13.wireOp",EDGE,"E282"),sQuery(id+"F13.wireOp",EDGE,"E283"),sQuery(id+"F13.wireOp",EDGE,"E284"),sQuery(id+"F13.wireOp",EDGE,"E285"),sQuery(id+"F13.wireOp",EDGE,"E286"),sQuery(id+"F13.wireOp",EDGE,"E287"),sQuery(id+"F13.wireOp",EDGE,"E288"),sQuery(id+"F13.wireOp",EDGE,"E289"),sQuery(id+"F13.wireOp",EDGE,"E290"),sQuery(id+"F13.wireOp",EDGE,"E291"),sQuery(id+"F13.wireOp",EDGE,"E292"),sQuery(id+"F13.wireOp",EDGE,"E293"),sQuery(id+"F13.wireOp",EDGE,"E294"),sQuery(id+"F13.wireOp",EDGE,"E295"),sQuery(id+"F13.wireOp",EDGE,"E296"),sQuery(id+"F13.wireOp",EDGE,"E297"),sQuery(id+"F13.wireOp",EDGE,"E298"),sQuery(id+"F13.wireOp",EDGE,"E299"),sQuery(id+"F13.wireOp",EDGE,"E300"),sQuery(id+"F13.wireOp",EDGE,"E301"),sQuery(id+"F13.wireOp",EDGE,"E302"),sQuery(id+"F13.wireOp",EDGE,"E303"),sQuery(id+"F13.wireOp",EDGE,"E304"),sQuery(id+"F13.wireOp",EDGE,"E305"),sQuery(id+"F13.wireOp",EDGE,"E306"),sQuery(id+"F13.wireOp",EDGE,"E307"),sQuery(id+"F13.wireOp",EDGE,"E308"),sQuery(id+"F13.wireOp",EDGE,"E309"),sQuery(id+"F13.wireOp",EDGE,"E310"),sQuery(id+"F13.wireOp",EDGE,"E311"),sQuery(id+"F13.wireOp",EDGE,"E312"),sQuery(id+"F13.wireOp",EDGE,"E313"),sQuery(id+"F13.wireOp",EDGE,"E314"),sQuery(id+"F13.wireOp",EDGE,"E316"),sQuery(id+"F13.wireOp",EDGE,"E317"),sQuery(id+"F13.wireOp",EDGE,"E318"),sQuery(id+"F13.wireOp",EDGE,"E319"),sQuery(id+"F13.wireOp",EDGE,"E320"),sQuery(id+"F13.wireOp",EDGE,"E321"),sQuery(id+"F13.wireOp",EDGE,"E322"),sQuery(id+"F13.wireOp",EDGE,"E323"),sQuery(id+"F13.wireOp",EDGE,"E324"),sQuery(id+"F13.wireOp",EDGE,"E325"),sQuery(id+"F13.wireOp",EDGE,"E326"),sQuery(id+"F13.wireOp",EDGE,"E327"),sQuery(id+"F13.wireOp",EDGE,"E328"),sQuery(id+"F13.wireOp",EDGE,"E329"),sQuery(id+"F13.wireOp",EDGE,"E330"),sQuery(id+"F13.wireOp",EDGE,"E331"),sQuery(id+"F13.wireOp",EDGE,"E332"),sQuery(id+"F13.wireOp",EDGE,"E333"),sQuery(id+"F13.wireOp",EDGE,"E334"),sQuery(id+"F13.wireOp",EDGE,"E335"),sQuery(id+"F13.wireOp",EDGE,"E339"),sQuery(id+"F13.wireOp",EDGE,"E340"),sQuery(id+"F13.wireOp",EDGE,"E341"),sQuery(id+"F13.wireOp",EDGE,"E342"),sQuery(id+"F13.wireOp",EDGE,"E343"),sQuery(id+"F13.wireOp",EDGE,"E344"),sQuery(id+"F13.wireOp",EDGE,"E345"),sQuery(id+"F13.wireOp",EDGE,"E346"),sQuery(id+"F13.wireOp",EDGE,"E347"),sQuery(id+"F13.wireOp",EDGE,"E348"),sQuery(id+"F13.wireOp",EDGE,"E349"),sQuery(id+"F13.wireOp",EDGE,"E350"),sQuery(id+"F13.wireOp",EDGE,"E351"),sQuery(id+"F13.wireOp",EDGE,"E352"),sQuery(id+"F13.wireOp",EDGE,"E353"),sQuery(id+"F13.wireOp",EDGE,"E354"),sQuery(id+"F13.wireOp",EDGE,"E355"),sQuery(id+"F13.wireOp",EDGE,"E356"),sQuery(id+"F13.wireOp",EDGE,"E357"),sQuery(id+"F13.wireOp",EDGE,"E358"),sQuery(id+"F13.wireOp",EDGE,"E359"),sQuery(id+"F13.wireOp",EDGE,"E362"),sQuery(id+"F13.wireOp",EDGE,"E363"),sQuery(id+"F13.wireOp",EDGE,"E364"),sQuery(id+"F13.wireOp",EDGE,"E365"),sQuery(id+"F13.wireOp",EDGE,"E366"),sQuery(id+"F13.wireOp",EDGE,"E367"),sQuery(id+"F13.wireOp",EDGE,"E368"),sQuery(id+"F13.wireOp",EDGE,"E369"),sQuery(id+"F13.wireOp",EDGE,"E370"),sQuery(id+"F13.wireOp",EDGE,"E371"),sQuery(id+"F13.wireOp",EDGE,"E372"),sQuery(id+"F13.wireOp",EDGE,"E373"),sQuery(id+"F13.wireOp",EDGE,"E374"),sQuery(id+"F13.wireOp",EDGE,"E375"),sQuery(id+"F13.wireOp",EDGE,"E376"),sQuery(id+"F13.wireOp",EDGE,"E377"),sQuery(id+"F13.wireOp",EDGE,"E378"),sQuery(id+"F13.wireOp",EDGE,"E379"),sQuery(id+"F13.wireOp",EDGE,"E380"),sQuery(id+"F13.wireOp",EDGE,"E381"),sQuery(id+"F13.wireOp",EDGE,"E382"),sQuery(id+"F13.wireOp",EDGE,"E383"),sQuery(id+"F13.wireOp",EDGE,"E384"),sQuery(id+"F13.wireOp",EDGE,"E385"),sQuery(id+"F13.wireOp",EDGE,"E386"),sQuery(id+"F13.wireOp",EDGE,"E387"),sQuery(id+"F13.wireOp",EDGE,"E388"),sQuery(id+"F13.wireOp",EDGE,"E389"),sQuery(id+"F13.wireOp",EDGE,"E390"),sQuery(id+"F13.wireOp",EDGE,"E391"),sQuery(id+"F13.wireOp",EDGE,"E392")])]});
            var Q1;
            Q1=makeQuery(id+"F16.opPattern","COPY",BODY,{"derivedFrom":makeQuery(id+"F14.opExtrude","SWEPT_BODY",BODY,{"disambiguationData":[OSD([sQuery(id+"F13.wireOp",EDGE,"E266"),sQuery(id+"F13.wireOp",EDGE,"E267"),sQuery(id+"F13.wireOp",EDGE,"E268"),sQuery(id+"F13.wireOp",EDGE,"E269"),sQuery(id+"F13.wireOp",EDGE,"E270"),sQuery(id+"F13.wireOp",EDGE,"E271"),sQuery(id+"F13.wireOp",EDGE,"E272"),sQuery(id+"F13.wireOp",EDGE,"E273"),sQuery(id+"F13.wireOp",EDGE,"E274"),sQuery(id+"F13.wireOp",EDGE,"E275"),sQuery(id+"F13.wireOp",EDGE,"E276"),sQuery(id+"F13.wireOp",EDGE,"E277"),sQuery(id+"F13.wireOp",EDGE,"E278"),sQuery(id+"F13.wireOp",EDGE,"E279"),sQuery(id+"F13.wireOp",EDGE,"E280"),sQuery(id+"F13.wireOp",EDGE,"E281"),sQuery(id+"F13.wireOp",EDGE,"E282"),sQuery(id+"F13.wireOp",EDGE,"E283"),sQuery(id+"F13.wireOp",EDGE,"E284"),sQuery(id+"F13.wireOp",EDGE,"E285"),sQuery(id+"F13.wireOp",EDGE,"E286"),sQuery(id+"F13.wireOp",EDGE,"E287"),sQuery(id+"F13.wireOp",EDGE,"E288"),sQuery(id+"F13.wireOp",EDGE,"E289"),sQuery(id+"F13.wireOp",EDGE,"E290"),sQuery(id+"F13.wireOp",EDGE,"E291"),sQuery(id+"F13.wireOp",EDGE,"E292"),sQuery(id+"F13.wireOp",EDGE,"E293"),sQuery(id+"F13.wireOp",EDGE,"E294"),sQuery(id+"F13.wireOp",EDGE,"E295"),sQuery(id+"F13.wireOp",EDGE,"E296"),sQuery(id+"F13.wireOp",EDGE,"E297"),sQuery(id+"F13.wireOp",EDGE,"E298"),sQuery(id+"F13.wireOp",EDGE,"E299"),sQuery(id+"F13.wireOp",EDGE,"E300"),sQuery(id+"F13.wireOp",EDGE,"E301"),sQuery(id+"F13.wireOp",EDGE,"E302"),sQuery(id+"F13.wireOp",EDGE,"E303"),sQuery(id+"F13.wireOp",EDGE,"E304"),sQuery(id+"F13.wireOp",EDGE,"E305"),sQuery(id+"F13.wireOp",EDGE,"E306"),sQuery(id+"F13.wireOp",EDGE,"E307"),sQuery(id+"F13.wireOp",EDGE,"E308"),sQuery(id+"F13.wireOp",EDGE,"E309"),sQuery(id+"F13.wireOp",EDGE,"E310"),sQuery(id+"F13.wireOp",EDGE,"E311"),sQuery(id+"F13.wireOp",EDGE,"E312"),sQuery(id+"F13.wireOp",EDGE,"E313"),sQuery(id+"F13.wireOp",EDGE,"E314"),sQuery(id+"F13.wireOp",EDGE,"E316"),sQuery(id+"F13.wireOp",EDGE,"E317"),sQuery(id+"F13.wireOp",EDGE,"E318"),sQuery(id+"F13.wireOp",EDGE,"E319"),sQuery(id+"F13.wireOp",EDGE,"E320"),sQuery(id+"F13.wireOp",EDGE,"E321"),sQuery(id+"F13.wireOp",EDGE,"E322"),sQuery(id+"F13.wireOp",EDGE,"E323"),sQuery(id+"F13.wireOp",EDGE,"E324"),sQuery(id+"F13.wireOp",EDGE,"E325"),sQuery(id+"F13.wireOp",EDGE,"E326"),sQuery(id+"F13.wireOp",EDGE,"E327"),sQuery(id+"F13.wireOp",EDGE,"E328"),sQuery(id+"F13.wireOp",EDGE,"E329"),sQuery(id+"F13.wireOp",EDGE,"E330"),sQuery(id+"F13.wireOp",EDGE,"E331"),sQuery(id+"F13.wireOp",EDGE,"E332"),sQuery(id+"F13.wireOp",EDGE,"E333"),sQuery(id+"F13.wireOp",EDGE,"E334"),sQuery(id+"F13.wireOp",EDGE,"E335"),sQuery(id+"F13.wireOp",EDGE,"E339"),sQuery(id+"F13.wireOp",EDGE,"E340"),sQuery(id+"F13.wireOp",EDGE,"E341"),sQuery(id+"F13.wireOp",EDGE,"E342"),sQuery(id+"F13.wireOp",EDGE,"E343"),sQuery(id+"F13.wireOp",EDGE,"E344"),sQuery(id+"F13.wireOp",EDGE,"E345"),sQuery(id+"F13.wireOp",EDGE,"E346"),sQuery(id+"F13.wireOp",EDGE,"E347"),sQuery(id+"F13.wireOp",EDGE,"E348"),sQuery(id+"F13.wireOp",EDGE,"E349"),sQuery(id+"F13.wireOp",EDGE,"E350"),sQuery(id+"F13.wireOp",EDGE,"E351"),sQuery(id+"F13.wireOp",EDGE,"E352"),sQuery(id+"F13.wireOp",EDGE,"E353"),sQuery(id+"F13.wireOp",EDGE,"E354"),sQuery(id+"F13.wireOp",EDGE,"E355"),sQuery(id+"F13.wireOp",EDGE,"E356"),sQuery(id+"F13.wireOp",EDGE,"E357"),sQuery(id+"F13.wireOp",EDGE,"E358"),sQuery(id+"F13.wireOp",EDGE,"E359"),sQuery(id+"F13.wireOp",EDGE,"E362"),sQuery(id+"F13.wireOp",EDGE,"E363"),sQuery(id+"F13.wireOp",EDGE,"E364"),sQuery(id+"F13.wireOp",EDGE,"E365"),sQuery(id+"F13.wireOp",EDGE,"E366"),sQuery(id+"F13.wireOp",EDGE,"E367"),sQuery(id+"F13.wireOp",EDGE,"E368"),sQuery(id+"F13.wireOp",EDGE,"E369"),sQuery(id+"F13.wireOp",EDGE,"E370"),sQuery(id+"F13.wireOp",EDGE,"E371"),sQuery(id+"F13.wireOp",EDGE,"E372"),sQuery(id+"F13.wireOp",EDGE,"E373"),sQuery(id+"F13.wireOp",EDGE,"E374"),sQuery(id+"F13.wireOp",EDGE,"E375"),sQuery(id+"F13.wireOp",EDGE,"E376"),sQuery(id+"F13.wireOp",EDGE,"E377"),sQuery(id+"F13.wireOp",EDGE,"E378"),sQuery(id+"F13.wireOp",EDGE,"E379"),sQuery(id+"F13.wireOp",EDGE,"E380"),sQuery(id+"F13.wireOp",EDGE,"E381"),sQuery(id+"F13.wireOp",EDGE,"E382"),sQuery(id+"F13.wireOp",EDGE,"E383"),sQuery(id+"F13.wireOp",EDGE,"E384"),sQuery(id+"F13.wireOp",EDGE,"E385"),sQuery(id+"F13.wireOp",EDGE,"E386"),sQuery(id+"F13.wireOp",EDGE,"E387"),sQuery(id+"F13.wireOp",EDGE,"E388"),sQuery(id+"F13.wireOp",EDGE,"E389"),sQuery(id+"F13.wireOp",EDGE,"E390"),sQuery(id+"F13.wireOp",EDGE,"E391"),sQuery(id+"F13.wireOp",EDGE,"E392")])]}),"instanceName":"1"});
            transform(context, id + "F17", {"entities" : qUnion([Q0, Q1]), "transformType" : TransformType.TRANSLATION_3D, "dx" : -750 * mm, "dy" : 0 * mm, "dz" : 0 * mm, "makeCopy" : true});
        }
        {
            var Q0;
            Q0=makeQuery(id+"F14.opExtrude","SWEPT_BODY",BODY,{"disambiguationData":[OSD([sQuery(id+"F13.wireOp",EDGE,"E266"),sQuery(id+"F13.wireOp",EDGE,"E267"),sQuery(id+"F13.wireOp",EDGE,"E268"),sQuery(id+"F13.wireOp",EDGE,"E269"),sQuery(id+"F13.wireOp",EDGE,"E270"),sQuery(id+"F13.wireOp",EDGE,"E271"),sQuery(id+"F13.wireOp",EDGE,"E272"),sQuery(id+"F13.wireOp",EDGE,"E273"),sQuery(id+"F13.wireOp",EDGE,"E274"),sQuery(id+"F13.wireOp",EDGE,"E275"),sQuery(id+"F13.wireOp",EDGE,"E276"),sQuery(id+"F13.wireOp",EDGE,"E277"),sQuery(id+"F13.wireOp",EDGE,"E278"),sQuery(id+"F13.wireOp",EDGE,"E279"),sQuery(id+"F13.wireOp",EDGE,"E280"),sQuery(id+"F13.wireOp",EDGE,"E281"),sQuery(id+"F13.wireOp",EDGE,"E282"),sQuery(id+"F13.wireOp",EDGE,"E283"),sQuery(id+"F13.wireOp",EDGE,"E284"),sQuery(id+"F13.wireOp",EDGE,"E285"),sQuery(id+"F13.wireOp",EDGE,"E286"),sQuery(id+"F13.wireOp",EDGE,"E287"),sQuery(id+"F13.wireOp",EDGE,"E288"),sQuery(id+"F13.wireOp",EDGE,"E289"),sQuery(id+"F13.wireOp",EDGE,"E290"),sQuery(id+"F13.wireOp",EDGE,"E291"),sQuery(id+"F13.wireOp",EDGE,"E292"),sQuery(id+"F13.wireOp",EDGE,"E293"),sQuery(id+"F13.wireOp",EDGE,"E294"),sQuery(id+"F13.wireOp",EDGE,"E295"),sQuery(id+"F13.wireOp",EDGE,"E296"),sQuery(id+"F13.wireOp",EDGE,"E297"),sQuery(id+"F13.wireOp",EDGE,"E298"),sQuery(id+"F13.wireOp",EDGE,"E299"),sQuery(id+"F13.wireOp",EDGE,"E300"),sQuery(id+"F13.wireOp",EDGE,"E301"),sQuery(id+"F13.wireOp",EDGE,"E302"),sQuery(id+"F13.wireOp",EDGE,"E303"),sQuery(id+"F13.wireOp",EDGE,"E304"),sQuery(id+"F13.wireOp",EDGE,"E305"),sQuery(id+"F13.wireOp",EDGE,"E306"),sQuery(id+"F13.wireOp",EDGE,"E307"),sQuery(id+"F13.wireOp",EDGE,"E308"),sQuery(id+"F13.wireOp",EDGE,"E309"),sQuery(id+"F13.wireOp",EDGE,"E310"),sQuery(id+"F13.wireOp",EDGE,"E311"),sQuery(id+"F13.wireOp",EDGE,"E312"),sQuery(id+"F13.wireOp",EDGE,"E313"),sQuery(id+"F13.wireOp",EDGE,"E314"),sQuery(id+"F13.wireOp",EDGE,"E316"),sQuery(id+"F13.wireOp",EDGE,"E317"),sQuery(id+"F13.wireOp",EDGE,"E318"),sQuery(id+"F13.wireOp",EDGE,"E319"),sQuery(id+"F13.wireOp",EDGE,"E320"),sQuery(id+"F13.wireOp",EDGE,"E321"),sQuery(id+"F13.wireOp",EDGE,"E322"),sQuery(id+"F13.wireOp",EDGE,"E323"),sQuery(id+"F13.wireOp",EDGE,"E324"),sQuery(id+"F13.wireOp",EDGE,"E325"),sQuery(id+"F13.wireOp",EDGE,"E326"),sQuery(id+"F13.wireOp",EDGE,"E327"),sQuery(id+"F13.wireOp",EDGE,"E328"),sQuery(id+"F13.wireOp",EDGE,"E329"),sQuery(id+"F13.wireOp",EDGE,"E330"),sQuery(id+"F13.wireOp",EDGE,"E331"),sQuery(id+"F13.wireOp",EDGE,"E332"),sQuery(id+"F13.wireOp",EDGE,"E333"),sQuery(id+"F13.wireOp",EDGE,"E334"),sQuery(id+"F13.wireOp",EDGE,"E335"),sQuery(id+"F13.wireOp",EDGE,"E339"),sQuery(id+"F13.wireOp",EDGE,"E340"),sQuery(id+"F13.wireOp",EDGE,"E341"),sQuery(id+"F13.wireOp",EDGE,"E342"),sQuery(id+"F13.wireOp",EDGE,"E343"),sQuery(id+"F13.wireOp",EDGE,"E344"),sQuery(id+"F13.wireOp",EDGE,"E345"),sQuery(id+"F13.wireOp",EDGE,"E346"),sQuery(id+"F13.wireOp",EDGE,"E347"),sQuery(id+"F13.wireOp",EDGE,"E348"),sQuery(id+"F13.wireOp",EDGE,"E349"),sQuery(id+"F13.wireOp",EDGE,"E350"),sQuery(id+"F13.wireOp",EDGE,"E351"),sQuery(id+"F13.wireOp",EDGE,"E352"),sQuery(id+"F13.wireOp",EDGE,"E353"),sQuery(id+"F13.wireOp",EDGE,"E354"),sQuery(id+"F13.wireOp",EDGE,"E355"),sQuery(id+"F13.wireOp",EDGE,"E356"),sQuery(id+"F13.wireOp",EDGE,"E357"),sQuery(id+"F13.wireOp",EDGE,"E358"),sQuery(id+"F13.wireOp",EDGE,"E359"),sQuery(id+"F13.wireOp",EDGE,"E362"),sQuery(id+"F13.wireOp",EDGE,"E363"),sQuery(id+"F13.wireOp",EDGE,"E364"),sQuery(id+"F13.wireOp",EDGE,"E365"),sQuery(id+"F13.wireOp",EDGE,"E366"),sQuery(id+"F13.wireOp",EDGE,"E367"),sQuery(id+"F13.wireOp",EDGE,"E368"),sQuery(id+"F13.wireOp",EDGE,"E369"),sQuery(id+"F13.wireOp",EDGE,"E370"),sQuery(id+"F13.wireOp",EDGE,"E371"),sQuery(id+"F13.wireOp",EDGE,"E372"),sQuery(id+"F13.wireOp",EDGE,"E373"),sQuery(id+"F13.wireOp",EDGE,"E374"),sQuery(id+"F13.wireOp",EDGE,"E375"),sQuery(id+"F13.wireOp",EDGE,"E376"),sQuery(id+"F13.wireOp",EDGE,"E377"),sQuery(id+"F13.wireOp",EDGE,"E378"),sQuery(id+"F13.wireOp",EDGE,"E379"),sQuery(id+"F13.wireOp",EDGE,"E380"),sQuery(id+"F13.wireOp",EDGE,"E381"),sQuery(id+"F13.wireOp",EDGE,"E382"),sQuery(id+"F13.wireOp",EDGE,"E383"),sQuery(id+"F13.wireOp",EDGE,"E384"),sQuery(id+"F13.wireOp",EDGE,"E385"),sQuery(id+"F13.wireOp",EDGE,"E386"),sQuery(id+"F13.wireOp",EDGE,"E387"),sQuery(id+"F13.wireOp",EDGE,"E388"),sQuery(id+"F13.wireOp",EDGE,"E389"),sQuery(id+"F13.wireOp",EDGE,"E390"),sQuery(id+"F13.wireOp",EDGE,"E391"),sQuery(id+"F13.wireOp",EDGE,"E392")])]});
            var Q1;
            Q1=makeQuery(id+"F16.opPattern","COPY",BODY,{"derivedFrom":makeQuery(id+"F14.opExtrude","SWEPT_BODY",BODY,{"disambiguationData":[OSD([sQuery(id+"F13.wireOp",EDGE,"E266"),sQuery(id+"F13.wireOp",EDGE,"E267"),sQuery(id+"F13.wireOp",EDGE,"E268"),sQuery(id+"F13.wireOp",EDGE,"E269"),sQuery(id+"F13.wireOp",EDGE,"E270"),sQuery(id+"F13.wireOp",EDGE,"E271"),sQuery(id+"F13.wireOp",EDGE,"E272"),sQuery(id+"F13.wireOp",EDGE,"E273"),sQuery(id+"F13.wireOp",EDGE,"E274"),sQuery(id+"F13.wireOp",EDGE,"E275"),sQuery(id+"F13.wireOp",EDGE,"E276"),sQuery(id+"F13.wireOp",EDGE,"E277"),sQuery(id+"F13.wireOp",EDGE,"E278"),sQuery(id+"F13.wireOp",EDGE,"E279"),sQuery(id+"F13.wireOp",EDGE,"E280"),sQuery(id+"F13.wireOp",EDGE,"E281"),sQuery(id+"F13.wireOp",EDGE,"E282"),sQuery(id+"F13.wireOp",EDGE,"E283"),sQuery(id+"F13.wireOp",EDGE,"E284"),sQuery(id+"F13.wireOp",EDGE,"E285"),sQuery(id+"F13.wireOp",EDGE,"E286"),sQuery(id+"F13.wireOp",EDGE,"E287"),sQuery(id+"F13.wireOp",EDGE,"E288"),sQuery(id+"F13.wireOp",EDGE,"E289"),sQuery(id+"F13.wireOp",EDGE,"E290"),sQuery(id+"F13.wireOp",EDGE,"E291"),sQuery(id+"F13.wireOp",EDGE,"E292"),sQuery(id+"F13.wireOp",EDGE,"E293"),sQuery(id+"F13.wireOp",EDGE,"E294"),sQuery(id+"F13.wireOp",EDGE,"E295"),sQuery(id+"F13.wireOp",EDGE,"E296"),sQuery(id+"F13.wireOp",EDGE,"E297"),sQuery(id+"F13.wireOp",EDGE,"E298"),sQuery(id+"F13.wireOp",EDGE,"E299"),sQuery(id+"F13.wireOp",EDGE,"E300"),sQuery(id+"F13.wireOp",EDGE,"E301"),sQuery(id+"F13.wireOp",EDGE,"E302"),sQuery(id+"F13.wireOp",EDGE,"E303"),sQuery(id+"F13.wireOp",EDGE,"E304"),sQuery(id+"F13.wireOp",EDGE,"E305"),sQuery(id+"F13.wireOp",EDGE,"E306"),sQuery(id+"F13.wireOp",EDGE,"E307"),sQuery(id+"F13.wireOp",EDGE,"E308"),sQuery(id+"F13.wireOp",EDGE,"E309"),sQuery(id+"F13.wireOp",EDGE,"E310"),sQuery(id+"F13.wireOp",EDGE,"E311"),sQuery(id+"F13.wireOp",EDGE,"E312"),sQuery(id+"F13.wireOp",EDGE,"E313"),sQuery(id+"F13.wireOp",EDGE,"E314"),sQuery(id+"F13.wireOp",EDGE,"E316"),sQuery(id+"F13.wireOp",EDGE,"E317"),sQuery(id+"F13.wireOp",EDGE,"E318"),sQuery(id+"F13.wireOp",EDGE,"E319"),sQuery(id+"F13.wireOp",EDGE,"E320"),sQuery(id+"F13.wireOp",EDGE,"E321"),sQuery(id+"F13.wireOp",EDGE,"E322"),sQuery(id+"F13.wireOp",EDGE,"E323"),sQuery(id+"F13.wireOp",EDGE,"E324"),sQuery(id+"F13.wireOp",EDGE,"E325"),sQuery(id+"F13.wireOp",EDGE,"E326"),sQuery(id+"F13.wireOp",EDGE,"E327"),sQuery(id+"F13.wireOp",EDGE,"E328"),sQuery(id+"F13.wireOp",EDGE,"E329"),sQuery(id+"F13.wireOp",EDGE,"E330"),sQuery(id+"F13.wireOp",EDGE,"E331"),sQuery(id+"F13.wireOp",EDGE,"E332"),sQuery(id+"F13.wireOp",EDGE,"E333"),sQuery(id+"F13.wireOp",EDGE,"E334"),sQuery(id+"F13.wireOp",EDGE,"E335"),sQuery(id+"F13.wireOp",EDGE,"E339"),sQuery(id+"F13.wireOp",EDGE,"E340"),sQuery(id+"F13.wireOp",EDGE,"E341"),sQuery(id+"F13.wireOp",EDGE,"E342"),sQuery(id+"F13.wireOp",EDGE,"E343"),sQuery(id+"F13.wireOp",EDGE,"E344"),sQuery(id+"F13.wireOp",EDGE,"E345"),sQuery(id+"F13.wireOp",EDGE,"E346"),sQuery(id+"F13.wireOp",EDGE,"E347"),sQuery(id+"F13.wireOp",EDGE,"E348"),sQuery(id+"F13.wireOp",EDGE,"E349"),sQuery(id+"F13.wireOp",EDGE,"E350"),sQuery(id+"F13.wireOp",EDGE,"E351"),sQuery(id+"F13.wireOp",EDGE,"E352"),sQuery(id+"F13.wireOp",EDGE,"E353"),sQuery(id+"F13.wireOp",EDGE,"E354"),sQuery(id+"F13.wireOp",EDGE,"E355"),sQuery(id+"F13.wireOp",EDGE,"E356"),sQuery(id+"F13.wireOp",EDGE,"E357"),sQuery(id+"F13.wireOp",EDGE,"E358"),sQuery(id+"F13.wireOp",EDGE,"E359"),sQuery(id+"F13.wireOp",EDGE,"E362"),sQuery(id+"F13.wireOp",EDGE,"E363"),sQuery(id+"F13.wireOp",EDGE,"E364"),sQuery(id+"F13.wireOp",EDGE,"E365"),sQuery(id+"F13.wireOp",EDGE,"E366"),sQuery(id+"F13.wireOp",EDGE,"E367"),sQuery(id+"F13.wireOp",EDGE,"E368"),sQuery(id+"F13.wireOp",EDGE,"E369"),sQuery(id+"F13.wireOp",EDGE,"E370"),sQuery(id+"F13.wireOp",EDGE,"E371"),sQuery(id+"F13.wireOp",EDGE,"E372"),sQuery(id+"F13.wireOp",EDGE,"E373"),sQuery(id+"F13.wireOp",EDGE,"E374"),sQuery(id+"F13.wireOp",EDGE,"E375"),sQuery(id+"F13.wireOp",EDGE,"E376"),sQuery(id+"F13.wireOp",EDGE,"E377"),sQuery(id+"F13.wireOp",EDGE,"E378"),sQuery(id+"F13.wireOp",EDGE,"E379"),sQuery(id+"F13.wireOp",EDGE,"E380"),sQuery(id+"F13.wireOp",EDGE,"E381"),sQuery(id+"F13.wireOp",EDGE,"E382"),sQuery(id+"F13.wireOp",EDGE,"E383"),sQuery(id+"F13.wireOp",EDGE,"E384"),sQuery(id+"F13.wireOp",EDGE,"E385"),sQuery(id+"F13.wireOp",EDGE,"E386"),sQuery(id+"F13.wireOp",EDGE,"E387"),sQuery(id+"F13.wireOp",EDGE,"E388"),sQuery(id+"F13.wireOp",EDGE,"E389"),sQuery(id+"F13.wireOp",EDGE,"E390"),sQuery(id+"F13.wireOp",EDGE,"E391"),sQuery(id+"F13.wireOp",EDGE,"E392")])]}),"instanceName":"1"});
            transform(context, id + "F18", {"entities" : qUnion([Q0, Q1]), "transformType" : TransformType.TRANSLATION_3D, "dx" : -353 * mm, "dy" : 0 * mm, "dz" : 0 * mm, "makeCopy" : true});
        }
    });
